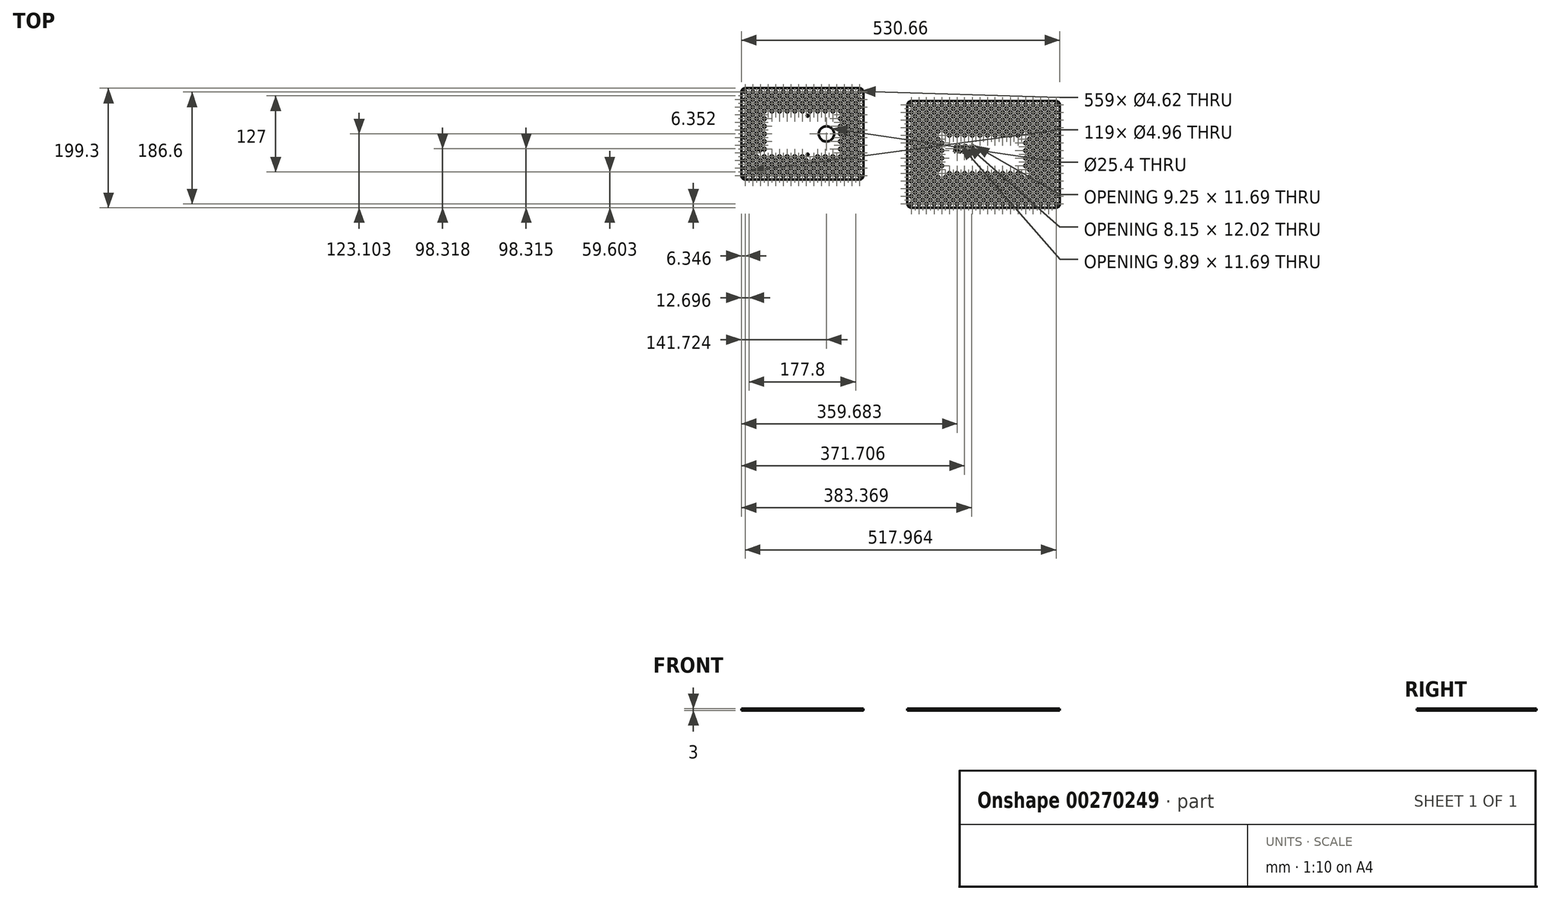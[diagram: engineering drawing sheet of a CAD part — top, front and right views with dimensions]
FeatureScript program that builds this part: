
annotation { "Feature Type Name" : "Feature", "Feature Type Description" : "" }
export const myFeature = defineFeature(function(context is Context, id is Id, definition is map)
    precondition{}
    {
        {
            var Q0;
            Q0=qCreatedBy(makeId("Top.planeOp"),FACE);
            var sketch = newSketch(context, id + "F0", { "sketchPlane" : qUnion([Q0])});
            skLineSegment(sketch, "E0.bottom", {"start": v(-123.65, 33.77) * mm, "end": v(-33.15, 33.77) * mm});
            skLineSegment(sketch, "E0.top", {"start": v(-123.65, -51.03) * mm, "end": v(-106.77, -51.03) * mm});
            skLineSegment(sketch, "E0.left", {"start": v(-123.65, 33.77) * mm, "end": v(-123.65, -51.03) * mm});
            skLineSegment(sketch, "E0.right", {"start": v(-33.15, 33.77) * mm, "end": v(-33.15, 7.9) * mm});
            skLineSegment(sketch, "E1", {"start": v(-38.6, 21.73) * mm, "end": v(-38.6, -43.27) * mm});
            skLineSegment(sketch, "E2", {"start": v(-117.57, 21.73) * mm, "end": v(-38.6, 21.73) * mm});
            skLineSegment(sketch, "E3", {"start": v(-38.6, 21.73) * mm, "end": v(-38.6, 33.77) * mm});
            skLineSegment(sketch, "E4", {"start": v(-38.6, -43.27) * mm, "end": v(-38.6, -51.03) * mm});
            skLineSegment(sketch, "E5", {"start": v(-37.02, -43.27) * mm, "end": v(-38.6, -43.27) * mm});
            skLineSegment(sketch, "E6", {"start": v(-117.57, -43.27) * mm, "end": v(-117.57, -36.09) * mm});
            skLineSegment(sketch, "E7", {"start": v(-117.57, -36.09) * mm, "end": v(-117.57, 21.73) * mm});
            skCircle(sketch, "E8", {"center": v(-117.57, -36.09) * mm, "radius": 1.59 * mm});
            skCircle(sketch, "E9", {"center": v(-38.6, 21.73) * mm, "radius": 1.59 * mm});
            skCircle(sketch, "E10", {"center": v(-38.6, -43.27) * mm, "radius": 1.59 * mm});
            skLineSegment(sketch, "E11.bottom", {"start": v(-142.7, 67.57) * mm, "end": v(47.8, 67.57) * mm});
            skLineSegment(sketch, "E11.top", {"start": v(-142.7, -84.83) * mm, "end": v(47.8, -84.83) * mm});
            skLineSegment(sketch, "E11.left", {"start": v(-149.05, 61.22) * mm, "end": v(-149.05, -78.48) * mm});
            skLineSegment(sketch, "E11.right", {"start": v(54.15, 61.22) * mm, "end": v(54.15, -78.48) * mm});
            skPoint(sketch, "E12", {"position": v(-106.77, -51.03) * mm});
            skPoint(sketch, "E13", {"position": v(-98.6, -51.03) * mm});
            skLineSegment(sketch, "E14.trimOffspring", {"start": v(-98.6, -51.03) * mm, "end": v(-33.15, -51.03) * mm});
            skPoint(sketch, "E15", {"position": v(-33.15, 7.9) * mm});
            skPoint(sketch, "E16", {"position": v(-33.15, -0.84) * mm});
            skLineSegment(sketch, "E17.trimOffspring", {"start": v(-33.15, -0.84) * mm, "end": v(-33.15, -51.03) * mm});
            skLineSegment(sketch, "E18", {"start": v(-149.05, -8.63) * mm, "end": v(-123.65, -8.63) * mm});
            skPoint(sketch, "E19", {"position": v(-90.24, -8.63) * mm});
            skPoint(sketch, "E20", {"position": v(-81.22, -8.63) * mm});
            skPoint(sketch, "E21", {"position": v(-47.45, -38.9) * mm});
            skLineSegment(sketch, "E22.trimOffspring", {"start": v(-81.22, -8.63) * mm, "end": v(-38.6, -8.63) * mm});
            skLineSegment(sketch, "E23.trimOffspring", {"start": v(-47.45, -38.9) * mm, "end": v(-47.45, -84.83) * mm});
            skLineSegment(sketch, "E24.trimOffspring", {"start": v(-117.57, -8.63) * mm, "end": v(-90.24, -8.63) * mm});
            skLineSegment(sketch, "E25.trimOffspring", {"start": v(-33.15, -8.63) * mm, "end": v(54.15, -8.63) * mm});
            skCircle(sketch, "E26", {"center": v(-7.33, -8.63) * mm, "radius": 12.7 * mm});
            skPoint(sketch, "E27.visualSharp", {"position": v(54.15, 67.57) * mm});
            skArc(sketch, "E27.filletArc", {"start": v(54.15, 61.22) * mm, "mid": v(52.29, 65.71) * mm, "end": v(47.8, 67.57) * mm});
            skPoint(sketch, "E28.visualSharp", {"position": v(-149.05, 67.57) * mm});
            skArc(sketch, "E28.filletArc", {"start": v(-142.7, 67.57) * mm, "mid": v(-147.2, 65.71) * mm, "end": v(-149.05, 61.22) * mm});
            skPoint(sketch, "E29.visualSharp", {"position": v(-149.05, -84.83) * mm});
            skArc(sketch, "E29.filletArc", {"start": v(-149.05, -78.48) * mm, "mid": v(-147.2, -82.97) * mm, "end": v(-142.7, -84.83) * mm});
            skPoint(sketch, "E30.visualSharp", {"position": v(54.15, -84.83) * mm});
            skArc(sketch, "E30.filletArc", {"start": v(47.8, -84.83) * mm, "mid": v(52.29, -82.97) * mm, "end": v(54.15, -78.48) * mm});
            skSolve(sketch);
        }
        {
            var Q0;
            Q0 = qSketchRegion(id + "F0", true);
            extrude(context, id + "F1", {"entities" : qUnion([Q0]), "depth" : 3 * mm});
        }
        {
            var Q0;
            Q0=makeQuery(id+"F1.opExtrude","CAP_FACE",FACE,{"disambiguationData":[OSD([sQuery(id+"F0.wireOp",EDGE,"E8"),sQuery(id+"F0.wireOp",EDGE,"E9"),sQuery(id+"F0.wireOp",EDGE,"E10"),sQuery(id+"F0.wireOp",EDGE,"E11.bottom"),sQuery(id+"F0.wireOp",EDGE,"E11.top"),sQuery(id+"F0.wireOp",EDGE,"E11.left"),sQuery(id+"F0.wireOp",EDGE,"E11.right"),sQuery(id+"F0.wireOp",EDGE,"E26")])],"isStart":false});
            var sketch = newSketch(context, id + "F2", { "sketchPlane" : qUnion([Q0])});
            skCircle(sketch, "E31", {"center": v(-142.7, 61.22) * mm, "radius": 2.31 * mm});
            skLineSegment(sketch, "E32", {"start": v(-142.7, 61.22) * mm, "end": v(-142.7, 67.57) * mm});
            skLineSegment(sketch, "E33", {"start": v(-142.7, 61.22) * mm, "end": v(-149.05, 61.22) * mm});
            skCircle(sketch, "E34.0.1.0", {"center": v(-142.7, 48.52) * mm, "radius": 2.31 * mm});
            skCircle(sketch, "E34.0.2.0", {"center": v(-142.7, 35.82) * mm, "radius": 2.31 * mm});
            skCircle(sketch, "E34.0.3.0", {"center": v(-142.7, 23.12) * mm, "radius": 2.31 * mm});
            skCircle(sketch, "E34.0.4.0", {"center": v(-142.7, 10.42) * mm, "radius": 2.31 * mm});
            skCircle(sketch, "E34.0.5.0", {"center": v(-142.7, -2.28) * mm, "radius": 2.31 * mm});
            skCircle(sketch, "E34.0.6.0", {"center": v(-142.7, -14.98) * mm, "radius": 2.31 * mm});
            skCircle(sketch, "E34.0.7.0", {"center": v(-142.7, -27.68) * mm, "radius": 2.31 * mm});
            skCircle(sketch, "E34.0.8.0", {"center": v(-142.7, -40.38) * mm, "radius": 2.31 * mm});
            skCircle(sketch, "E34.0.9.0", {"center": v(-142.7, -53.08) * mm, "radius": 2.31 * mm});
            skCircle(sketch, "E34.0.10.0", {"center": v(-142.7, -65.78) * mm, "radius": 2.31 * mm});
            skCircle(sketch, "E34.0.11.0", {"center": v(-142.7, -78.48) * mm, "radius": 2.31 * mm});
            skCircle(sketch, "E34.1.0.0", {"center": v(-130, 61.22) * mm, "radius": 2.31 * mm});
            skCircle(sketch, "E34.1.1.0", {"center": v(-130, 48.52) * mm, "radius": 2.31 * mm});
            skCircle(sketch, "E34.1.2.0", {"center": v(-130, 35.82) * mm, "radius": 2.31 * mm});
            skCircle(sketch, "E34.1.3.0", {"center": v(-130, 23.12) * mm, "radius": 2.31 * mm});
            skCircle(sketch, "E34.1.4.0", {"center": v(-130, 10.42) * mm, "radius": 2.31 * mm});
            skCircle(sketch, "E34.1.5.0", {"center": v(-130, -2.28) * mm, "radius": 2.31 * mm});
            skCircle(sketch, "E34.1.6.0", {"center": v(-130, -14.98) * mm, "radius": 2.31 * mm});
            skCircle(sketch, "E34.1.7.0", {"center": v(-130, -27.68) * mm, "radius": 2.31 * mm});
            skCircle(sketch, "E34.1.8.0", {"center": v(-130, -40.38) * mm, "radius": 2.31 * mm});
            skCircle(sketch, "E34.1.9.0", {"center": v(-130, -53.08) * mm, "radius": 2.31 * mm});
            skCircle(sketch, "E34.1.10.0", {"center": v(-130, -65.78) * mm, "radius": 2.31 * mm});
            skCircle(sketch, "E34.1.11.0", {"center": v(-130, -78.48) * mm, "radius": 2.31 * mm});
            skCircle(sketch, "E34.2.0.0", {"center": v(-117.3, 61.22) * mm, "radius": 2.31 * mm});
            skCircle(sketch, "E34.2.1.0", {"center": v(-117.3, 48.52) * mm, "radius": 2.31 * mm});
            skCircle(sketch, "E34.2.2.0", {"center": v(-117.3, 35.82) * mm, "radius": 2.31 * mm});
            skCircle(sketch, "E34.2.3.0", {"center": v(-117.3, 23.12) * mm, "radius": 2.31 * mm});
            skCircle(sketch, "E34.2.4.0", {"center": v(-117.3, 10.42) * mm, "radius": 2.31 * mm});
            skCircle(sketch, "E34.2.5.0", {"center": v(-117.3, -2.28) * mm, "radius": 2.31 * mm});
            skCircle(sketch, "E34.2.6.0", {"center": v(-117.3, -14.98) * mm, "radius": 2.31 * mm});
            skCircle(sketch, "E34.2.7.0", {"center": v(-117.3, -27.68) * mm, "radius": 2.31 * mm});
            skCircle(sketch, "E34.2.9.0", {"center": v(-117.3, -53.08) * mm, "radius": 2.31 * mm});
            skCircle(sketch, "E34.2.10.0", {"center": v(-117.3, -65.78) * mm, "radius": 2.31 * mm});
            skCircle(sketch, "E34.2.11.0", {"center": v(-117.3, -78.48) * mm, "radius": 2.31 * mm});
            skCircle(sketch, "E34.3.0.0", {"center": v(-104.6, 61.22) * mm, "radius": 2.31 * mm});
            skCircle(sketch, "E34.3.1.0", {"center": v(-104.6, 48.52) * mm, "radius": 2.31 * mm});
            skCircle(sketch, "E34.3.2.0", {"center": v(-104.6, 35.82) * mm, "radius": 2.31 * mm});
            skCircle(sketch, "E34.3.9.0", {"center": v(-104.6, -53.08) * mm, "radius": 2.31 * mm});
            skCircle(sketch, "E34.3.10.0", {"center": v(-104.6, -65.78) * mm, "radius": 2.31 * mm});
            skCircle(sketch, "E34.3.11.0", {"center": v(-104.6, -78.48) * mm, "radius": 2.31 * mm});
            skCircle(sketch, "E34.4.0.0", {"center": v(-91.9, 61.22) * mm, "radius": 2.31 * mm});
            skCircle(sketch, "E34.4.1.0", {"center": v(-91.9, 48.52) * mm, "radius": 2.31 * mm});
            skCircle(sketch, "E34.4.2.0", {"center": v(-91.9, 35.82) * mm, "radius": 2.31 * mm});
            skCircle(sketch, "E34.4.9.0", {"center": v(-91.9, -53.08) * mm, "radius": 2.31 * mm});
            skCircle(sketch, "E34.4.10.0", {"center": v(-91.9, -65.78) * mm, "radius": 2.31 * mm});
            skCircle(sketch, "E34.4.11.0", {"center": v(-91.9, -78.48) * mm, "radius": 2.31 * mm});
            skCircle(sketch, "E34.5.0.0", {"center": v(-79.2, 61.22) * mm, "radius": 2.31 * mm});
            skCircle(sketch, "E34.5.1.0", {"center": v(-79.2, 48.52) * mm, "radius": 2.31 * mm});
            skCircle(sketch, "E34.5.2.0", {"center": v(-79.2, 35.82) * mm, "radius": 2.31 * mm});
            skCircle(sketch, "E34.5.9.0", {"center": v(-79.2, -53.08) * mm, "radius": 2.31 * mm});
            skCircle(sketch, "E34.5.10.0", {"center": v(-79.2, -65.78) * mm, "radius": 2.31 * mm});
            skCircle(sketch, "E34.5.11.0", {"center": v(-79.2, -78.48) * mm, "radius": 2.31 * mm});
            skCircle(sketch, "E34.6.0.0", {"center": v(-66.5, 61.22) * mm, "radius": 2.31 * mm});
            skCircle(sketch, "E34.6.1.0", {"center": v(-66.5, 48.52) * mm, "radius": 2.31 * mm});
            skCircle(sketch, "E34.6.2.0", {"center": v(-66.5, 35.82) * mm, "radius": 2.31 * mm});
            skCircle(sketch, "E34.6.9.0", {"center": v(-66.5, -53.08) * mm, "radius": 2.31 * mm});
            skCircle(sketch, "E34.6.10.0", {"center": v(-66.5, -65.78) * mm, "radius": 2.31 * mm});
            skCircle(sketch, "E34.6.11.0", {"center": v(-66.5, -78.48) * mm, "radius": 2.31 * mm});
            skCircle(sketch, "E34.7.0.0", {"center": v(-53.8, 61.22) * mm, "radius": 2.31 * mm});
            skCircle(sketch, "E34.7.1.0", {"center": v(-53.8, 48.52) * mm, "radius": 2.31 * mm});
            skCircle(sketch, "E34.7.2.0", {"center": v(-53.8, 35.82) * mm, "radius": 2.31 * mm});
            skCircle(sketch, "E34.7.9.0", {"center": v(-53.8, -53.08) * mm, "radius": 2.31 * mm});
            skCircle(sketch, "E34.7.10.0", {"center": v(-53.8, -65.78) * mm, "radius": 2.31 * mm});
            skCircle(sketch, "E34.7.11.0", {"center": v(-53.8, -78.48) * mm, "radius": 2.31 * mm});
            skCircle(sketch, "E34.8.0.0", {"center": v(-41.1, 61.22) * mm, "radius": 2.31 * mm});
            skCircle(sketch, "E34.8.1.0", {"center": v(-41.1, 48.52) * mm, "radius": 2.31 * mm});
            skCircle(sketch, "E34.8.2.0", {"center": v(-41.1, 35.82) * mm, "radius": 2.31 * mm});
            skCircle(sketch, "E34.8.9.0", {"center": v(-41.1, -53.08) * mm, "radius": 2.31 * mm});
            skCircle(sketch, "E34.8.10.0", {"center": v(-41.1, -65.78) * mm, "radius": 2.31 * mm});
            skCircle(sketch, "E34.8.11.0", {"center": v(-41.1, -78.48) * mm, "radius": 2.31 * mm});
            skCircle(sketch, "E34.9.0.0", {"center": v(-28.4, 61.22) * mm, "radius": 2.31 * mm});
            skCircle(sketch, "E34.9.1.0", {"center": v(-28.4, 48.52) * mm, "radius": 2.31 * mm});
            skCircle(sketch, "E34.9.2.0", {"center": v(-28.4, 35.82) * mm, "radius": 2.31 * mm});
            skCircle(sketch, "E34.9.9.0", {"center": v(-28.4, -53.08) * mm, "radius": 2.31 * mm});
            skCircle(sketch, "E34.9.10.0", {"center": v(-28.4, -65.78) * mm, "radius": 2.31 * mm});
            skCircle(sketch, "E34.9.11.0", {"center": v(-28.4, -78.48) * mm, "radius": 2.31 * mm});
            skCircle(sketch, "E34.10.0.0", {"center": v(-15.7, 61.22) * mm, "radius": 2.31 * mm});
            skCircle(sketch, "E34.10.1.0", {"center": v(-15.7, 48.52) * mm, "radius": 2.31 * mm});
            skCircle(sketch, "E34.10.2.0", {"center": v(-15.7, 35.82) * mm, "radius": 2.31 * mm});
            skCircle(sketch, "E34.10.9.0", {"center": v(-15.7, -53.08) * mm, "radius": 2.31 * mm});
            skCircle(sketch, "E34.10.10.0", {"center": v(-15.7, -65.78) * mm, "radius": 2.31 * mm});
            skCircle(sketch, "E34.10.11.0", {"center": v(-15.7, -78.48) * mm, "radius": 2.31 * mm});
            skCircle(sketch, "E34.11.0.0", {"center": v(-3, 61.22) * mm, "radius": 2.31 * mm});
            skCircle(sketch, "E34.11.1.0", {"center": v(-3, 48.52) * mm, "radius": 2.31 * mm});
            skCircle(sketch, "E34.11.2.0", {"center": v(-3, 35.82) * mm, "radius": 2.31 * mm});
            skCircle(sketch, "E34.11.9.0", {"center": v(-3, -53.08) * mm, "radius": 2.31 * mm});
            skCircle(sketch, "E34.11.10.0", {"center": v(-3, -65.78) * mm, "radius": 2.31 * mm});
            skCircle(sketch, "E34.11.11.0", {"center": v(-3, -78.48) * mm, "radius": 2.31 * mm});
            skCircle(sketch, "E34.12.0.0", {"center": v(9.7, 61.22) * mm, "radius": 2.31 * mm});
            skCircle(sketch, "E34.12.1.0", {"center": v(9.7, 48.52) * mm, "radius": 2.31 * mm});
            skCircle(sketch, "E34.12.2.0", {"center": v(9.7, 35.82) * mm, "radius": 2.31 * mm});
            skCircle(sketch, "E34.12.9.0", {"center": v(9.7, -53.08) * mm, "radius": 2.31 * mm});
            skCircle(sketch, "E34.12.10.0", {"center": v(9.7, -65.78) * mm, "radius": 2.31 * mm});
            skCircle(sketch, "E34.12.11.0", {"center": v(9.7, -78.48) * mm, "radius": 2.31 * mm});
            skCircle(sketch, "E34.13.0.0", {"center": v(22.4, 61.22) * mm, "radius": 2.31 * mm});
            skCircle(sketch, "E34.13.1.0", {"center": v(22.4, 48.52) * mm, "radius": 2.31 * mm});
            skCircle(sketch, "E34.13.2.0", {"center": v(22.4, 35.82) * mm, "radius": 2.31 * mm});
            skCircle(sketch, "E34.13.3.0", {"center": v(22.4, 23.12) * mm, "radius": 2.31 * mm});
            skCircle(sketch, "E34.13.4.0", {"center": v(22.4, 10.42) * mm, "radius": 2.31 * mm});
            skCircle(sketch, "E34.13.5.0", {"center": v(22.4, -2.28) * mm, "radius": 2.31 * mm});
            skCircle(sketch, "E34.13.6.0", {"center": v(22.4, -14.98) * mm, "radius": 2.31 * mm});
            skCircle(sketch, "E34.13.7.0", {"center": v(22.4, -27.68) * mm, "radius": 2.31 * mm});
            skCircle(sketch, "E34.13.8.0", {"center": v(22.4, -40.38) * mm, "radius": 2.31 * mm});
            skCircle(sketch, "E34.13.9.0", {"center": v(22.4, -53.08) * mm, "radius": 2.31 * mm});
            skCircle(sketch, "E34.13.10.0", {"center": v(22.4, -65.78) * mm, "radius": 2.31 * mm});
            skCircle(sketch, "E34.13.11.0", {"center": v(22.4, -78.48) * mm, "radius": 2.31 * mm});
            skCircle(sketch, "E34.14.0.0", {"center": v(35.1, 61.22) * mm, "radius": 2.31 * mm});
            skCircle(sketch, "E34.14.1.0", {"center": v(35.1, 48.52) * mm, "radius": 2.31 * mm});
            skCircle(sketch, "E34.14.2.0", {"center": v(35.1, 35.82) * mm, "radius": 2.31 * mm});
            skCircle(sketch, "E34.14.3.0", {"center": v(35.1, 23.12) * mm, "radius": 2.31 * mm});
            skCircle(sketch, "E34.14.4.0", {"center": v(35.1, 10.42) * mm, "radius": 2.31 * mm});
            skCircle(sketch, "E34.14.5.0", {"center": v(35.1, -2.28) * mm, "radius": 2.31 * mm});
            skCircle(sketch, "E34.14.6.0", {"center": v(35.1, -14.98) * mm, "radius": 2.31 * mm});
            skCircle(sketch, "E34.14.7.0", {"center": v(35.1, -27.68) * mm, "radius": 2.31 * mm});
            skCircle(sketch, "E34.14.8.0", {"center": v(35.1, -40.38) * mm, "radius": 2.31 * mm});
            skCircle(sketch, "E34.14.9.0", {"center": v(35.1, -53.08) * mm, "radius": 2.31 * mm});
            skCircle(sketch, "E34.14.10.0", {"center": v(35.1, -65.78) * mm, "radius": 2.31 * mm});
            skCircle(sketch, "E34.14.11.0", {"center": v(35.1, -78.48) * mm, "radius": 2.31 * mm});
            skCircle(sketch, "E34.15.0.0", {"center": v(47.8, 61.22) * mm, "radius": 2.31 * mm});
            skCircle(sketch, "E34.15.1.0", {"center": v(47.8, 48.52) * mm, "radius": 2.31 * mm});
            skCircle(sketch, "E34.15.2.0", {"center": v(47.8, 35.82) * mm, "radius": 2.31 * mm});
            skCircle(sketch, "E34.15.3.0", {"center": v(47.8, 23.12) * mm, "radius": 2.31 * mm});
            skCircle(sketch, "E34.15.4.0", {"center": v(47.8, 10.42) * mm, "radius": 2.31 * mm});
            skCircle(sketch, "E34.15.5.0", {"center": v(47.8, -2.28) * mm, "radius": 2.31 * mm});
            skCircle(sketch, "E34.15.6.0", {"center": v(47.8, -14.98) * mm, "radius": 2.31 * mm});
            skCircle(sketch, "E34.15.7.0", {"center": v(47.8, -27.68) * mm, "radius": 2.31 * mm});
            skCircle(sketch, "E34.15.8.0", {"center": v(47.8, -40.38) * mm, "radius": 2.31 * mm});
            skCircle(sketch, "E34.15.9.0", {"center": v(47.8, -53.08) * mm, "radius": 2.31 * mm});
            skCircle(sketch, "E34.15.10.0", {"center": v(47.8, -65.78) * mm, "radius": 2.31 * mm});
            skCircle(sketch, "E34.15.11.0", {"center": v(47.8, -78.48) * mm, "radius": 2.31 * mm});
            skLineSegment(sketch, "E34.direction1", {"start": v(-142.7, 61.22) * mm, "end": v(-130, 61.22) * mm, "construction": true});
            skLineSegment(sketch, "E34.direction2", {"start": v(-142.7, 61.22) * mm, "end": v(-142.7, 48.52) * mm, "construction": true});
            skLineSegment(sketch, "E35", {"start": v(47.8, 61.22) * mm, "end": v(54.15, 61.22) * mm});
            skLineSegment(sketch, "E36", {"start": v(-142.7, -78.48) * mm, "end": v(-142.7, -84.83) * mm});
            skCircle(sketch, "E37", {"center": v(-136.35, 54.87) * mm, "radius": 2.48 * mm});
            skCircle(sketch, "E38.0.1.0", {"center": v(-136.35, 42.17) * mm, "radius": 2.48 * mm});
            skCircle(sketch, "E38.0.2.0", {"center": v(-136.35, 29.47) * mm, "radius": 2.48 * mm});
            skCircle(sketch, "E38.0.3.0", {"center": v(-136.35, 16.77) * mm, "radius": 2.48 * mm});
            skCircle(sketch, "E38.0.4.0", {"center": v(-136.35, 4.07) * mm, "radius": 2.48 * mm});
            skCircle(sketch, "E38.0.5.0", {"center": v(-136.35, -8.63) * mm, "radius": 2.48 * mm});
            skCircle(sketch, "E38.0.6.0", {"center": v(-136.35, -21.33) * mm, "radius": 2.48 * mm});
            skCircle(sketch, "E38.0.7.0", {"center": v(-136.35, -34.03) * mm, "radius": 2.48 * mm});
            skCircle(sketch, "E38.0.8.0", {"center": v(-136.35, -46.73) * mm, "radius": 2.48 * mm});
            skCircle(sketch, "E38.0.9.0", {"center": v(-136.35, -59.43) * mm, "radius": 2.48 * mm});
            skCircle(sketch, "E38.0.10.0", {"center": v(-136.35, -72.13) * mm, "radius": 2.48 * mm});
            skCircle(sketch, "E38.1.0.0", {"center": v(-123.65, 54.87) * mm, "radius": 2.48 * mm});
            skCircle(sketch, "E38.1.1.0", {"center": v(-123.65, 42.17) * mm, "radius": 2.48 * mm});
            skCircle(sketch, "E38.1.2.0", {"center": v(-123.65, 29.47) * mm, "radius": 2.48 * mm});
            skCircle(sketch, "E38.1.3.0", {"center": v(-123.65, 16.77) * mm, "radius": 2.48 * mm});
            skCircle(sketch, "E38.1.4.0", {"center": v(-123.65, 4.07) * mm, "radius": 2.48 * mm});
            skCircle(sketch, "E38.1.5.0", {"center": v(-123.65, -8.63) * mm, "radius": 2.48 * mm});
            skCircle(sketch, "E38.1.6.0", {"center": v(-123.65, -21.33) * mm, "radius": 2.48 * mm});
            skCircle(sketch, "E38.1.7.0", {"center": v(-123.65, -34.03) * mm, "radius": 2.48 * mm});
            skCircle(sketch, "E38.1.8.0", {"center": v(-123.65, -46.73) * mm, "radius": 2.48 * mm});
            skCircle(sketch, "E38.1.9.0", {"center": v(-123.65, -59.43) * mm, "radius": 2.48 * mm});
            skCircle(sketch, "E38.1.10.0", {"center": v(-123.65, -72.13) * mm, "radius": 2.48 * mm});
            skCircle(sketch, "E38.2.0.0", {"center": v(-110.95, 54.87) * mm, "radius": 2.48 * mm});
            skCircle(sketch, "E38.2.1.0", {"center": v(-110.95, 42.17) * mm, "radius": 2.48 * mm});
            skCircle(sketch, "E38.2.2.0", {"center": v(-110.95, 29.47) * mm, "radius": 2.48 * mm});
            skCircle(sketch, "E38.2.3.0", {"center": v(-110.95, 16.77) * mm, "radius": 2.48 * mm});
            skCircle(sketch, "E38.2.4.0", {"center": v(-110.95, 4.07) * mm, "radius": 2.48 * mm});
            skCircle(sketch, "E38.2.5.0", {"center": v(-110.95, -8.63) * mm, "radius": 2.48 * mm});
            skCircle(sketch, "E38.2.6.0", {"center": v(-110.95, -21.33) * mm, "radius": 2.48 * mm});
            skCircle(sketch, "E38.2.7.0", {"center": v(-110.95, -34.03) * mm, "radius": 2.48 * mm});
            skCircle(sketch, "E38.2.8.0", {"center": v(-110.95, -46.73) * mm, "radius": 2.48 * mm});
            skCircle(sketch, "E38.2.9.0", {"center": v(-110.95, -59.43) * mm, "radius": 2.48 * mm});
            skCircle(sketch, "E38.2.10.0", {"center": v(-110.95, -72.13) * mm, "radius": 2.48 * mm});
            skCircle(sketch, "E38.3.0.0", {"center": v(-98.25, 54.87) * mm, "radius": 2.48 * mm});
            skCircle(sketch, "E38.3.1.0", {"center": v(-98.25, 42.17) * mm, "radius": 2.48 * mm});
            skCircle(sketch, "E38.3.2.0", {"center": v(-98.25, 29.47) * mm, "radius": 2.48 * mm});
            skCircle(sketch, "E38.3.8.0", {"center": v(-98.25, -46.73) * mm, "radius": 2.48 * mm});
            skCircle(sketch, "E38.3.9.0", {"center": v(-98.25, -59.43) * mm, "radius": 2.48 * mm});
            skCircle(sketch, "E38.3.10.0", {"center": v(-98.25, -72.13) * mm, "radius": 2.48 * mm});
            skCircle(sketch, "E38.4.0.0", {"center": v(-85.55, 54.87) * mm, "radius": 2.48 * mm});
            skCircle(sketch, "E38.4.1.0", {"center": v(-85.55, 42.17) * mm, "radius": 2.48 * mm});
            skCircle(sketch, "E38.4.2.0", {"center": v(-85.55, 29.47) * mm, "radius": 2.48 * mm});
            skCircle(sketch, "E38.4.8.0", {"center": v(-85.55, -46.73) * mm, "radius": 2.48 * mm});
            skCircle(sketch, "E38.4.9.0", {"center": v(-85.55, -59.43) * mm, "radius": 2.48 * mm});
            skCircle(sketch, "E38.4.10.0", {"center": v(-85.55, -72.13) * mm, "radius": 2.48 * mm});
            skCircle(sketch, "E38.5.0.0", {"center": v(-72.85, 54.87) * mm, "radius": 2.48 * mm});
            skCircle(sketch, "E38.5.1.0", {"center": v(-72.85, 42.17) * mm, "radius": 2.48 * mm});
            skCircle(sketch, "E38.5.2.0", {"center": v(-72.85, 29.47) * mm, "radius": 2.48 * mm});
            skCircle(sketch, "E38.5.8.0", {"center": v(-72.85, -46.73) * mm, "radius": 2.48 * mm});
            skCircle(sketch, "E38.5.9.0", {"center": v(-72.85, -59.43) * mm, "radius": 2.48 * mm});
            skCircle(sketch, "E38.5.10.0", {"center": v(-72.85, -72.13) * mm, "radius": 2.48 * mm});
            skCircle(sketch, "E38.6.0.0", {"center": v(-60.15, 54.87) * mm, "radius": 2.48 * mm});
            skCircle(sketch, "E38.6.1.0", {"center": v(-60.15, 42.17) * mm, "radius": 2.48 * mm});
            skCircle(sketch, "E38.6.2.0", {"center": v(-60.15, 29.47) * mm, "radius": 2.48 * mm});
            skCircle(sketch, "E38.6.8.0", {"center": v(-60.15, -46.73) * mm, "radius": 2.48 * mm});
            skCircle(sketch, "E38.6.9.0", {"center": v(-60.15, -59.43) * mm, "radius": 2.48 * mm});
            skCircle(sketch, "E38.6.10.0", {"center": v(-60.15, -72.13) * mm, "radius": 2.48 * mm});
            skCircle(sketch, "E38.7.0.0", {"center": v(-47.45, 54.87) * mm, "radius": 2.48 * mm});
            skCircle(sketch, "E38.7.1.0", {"center": v(-47.45, 42.17) * mm, "radius": 2.48 * mm});
            skCircle(sketch, "E38.7.2.0", {"center": v(-47.45, 29.47) * mm, "radius": 2.48 * mm});
            skCircle(sketch, "E38.7.8.0", {"center": v(-47.45, -46.73) * mm, "radius": 2.48 * mm});
            skCircle(sketch, "E38.7.9.0", {"center": v(-47.45, -59.43) * mm, "radius": 2.48 * mm});
            skCircle(sketch, "E38.7.10.0", {"center": v(-47.45, -72.13) * mm, "radius": 2.48 * mm});
            skCircle(sketch, "E38.8.0.0", {"center": v(-34.75, 54.87) * mm, "radius": 2.48 * mm});
            skCircle(sketch, "E38.8.1.0", {"center": v(-34.75, 42.17) * mm, "radius": 2.48 * mm});
            skCircle(sketch, "E38.8.2.0", {"center": v(-34.75, 29.47) * mm, "radius": 2.48 * mm});
            skCircle(sketch, "E38.8.9.0", {"center": v(-34.75, -59.43) * mm, "radius": 2.48 * mm});
            skCircle(sketch, "E38.8.10.0", {"center": v(-34.75, -72.13) * mm, "radius": 2.48 * mm});
            skCircle(sketch, "E38.9.0.0", {"center": v(-22.05, 54.87) * mm, "radius": 2.48 * mm});
            skCircle(sketch, "E38.9.1.0", {"center": v(-22.05, 42.17) * mm, "radius": 2.48 * mm});
            skCircle(sketch, "E38.9.2.0", {"center": v(-22.05, 29.47) * mm, "radius": 2.48 * mm});
            skCircle(sketch, "E38.9.8.0", {"center": v(-22.05, -46.73) * mm, "radius": 2.48 * mm});
            skCircle(sketch, "E38.9.9.0", {"center": v(-22.05, -59.43) * mm, "radius": 2.48 * mm});
            skCircle(sketch, "E38.9.10.0", {"center": v(-22.05, -72.13) * mm, "radius": 2.48 * mm});
            skCircle(sketch, "E38.10.0.0", {"center": v(-9.35, 54.87) * mm, "radius": 2.48 * mm});
            skCircle(sketch, "E38.10.1.0", {"center": v(-9.35, 42.17) * mm, "radius": 2.48 * mm});
            skCircle(sketch, "E38.10.2.0", {"center": v(-9.35, 29.47) * mm, "radius": 2.48 * mm});
            skCircle(sketch, "E38.10.8.0", {"center": v(-9.35, -46.73) * mm, "radius": 2.48 * mm});
            skCircle(sketch, "E38.10.9.0", {"center": v(-9.35, -59.43) * mm, "radius": 2.48 * mm});
            skCircle(sketch, "E38.10.10.0", {"center": v(-9.35, -72.13) * mm, "radius": 2.48 * mm});
            skCircle(sketch, "E38.11.0.0", {"center": v(3.35, 54.87) * mm, "radius": 2.48 * mm});
            skCircle(sketch, "E38.11.1.0", {"center": v(3.35, 42.17) * mm, "radius": 2.48 * mm});
            skCircle(sketch, "E38.11.2.0", {"center": v(3.35, 29.47) * mm, "radius": 2.48 * mm});
            skCircle(sketch, "E38.11.8.0", {"center": v(3.35, -46.73) * mm, "radius": 2.48 * mm});
            skCircle(sketch, "E38.11.9.0", {"center": v(3.35, -59.43) * mm, "radius": 2.48 * mm});
            skCircle(sketch, "E38.11.10.0", {"center": v(3.35, -72.13) * mm, "radius": 2.48 * mm});
            skCircle(sketch, "E38.12.0.0", {"center": v(16.05, 54.87) * mm, "radius": 2.48 * mm});
            skCircle(sketch, "E38.12.1.0", {"center": v(16.05, 42.17) * mm, "radius": 2.48 * mm});
            skCircle(sketch, "E38.12.2.0", {"center": v(16.05, 29.47) * mm, "radius": 2.48 * mm});
            skCircle(sketch, "E38.12.3.0", {"center": v(16.05, 16.77) * mm, "radius": 2.48 * mm});
            skCircle(sketch, "E38.12.4.0", {"center": v(16.05, 4.07) * mm, "radius": 2.48 * mm});
            skCircle(sketch, "E38.12.5.0", {"center": v(16.05, -8.63) * mm, "radius": 2.48 * mm});
            skCircle(sketch, "E38.12.6.0", {"center": v(16.05, -21.33) * mm, "radius": 2.48 * mm});
            skCircle(sketch, "E38.12.7.0", {"center": v(16.05, -34.03) * mm, "radius": 2.48 * mm});
            skCircle(sketch, "E38.12.8.0", {"center": v(16.05, -46.73) * mm, "radius": 2.48 * mm});
            skCircle(sketch, "E38.12.9.0", {"center": v(16.05, -59.43) * mm, "radius": 2.48 * mm});
            skCircle(sketch, "E38.12.10.0", {"center": v(16.05, -72.13) * mm, "radius": 2.48 * mm});
            skCircle(sketch, "E38.13.0.0", {"center": v(28.75, 54.87) * mm, "radius": 2.48 * mm});
            skCircle(sketch, "E38.13.1.0", {"center": v(28.75, 42.17) * mm, "radius": 2.48 * mm});
            skCircle(sketch, "E38.13.2.0", {"center": v(28.75, 29.47) * mm, "radius": 2.48 * mm});
            skCircle(sketch, "E38.13.3.0", {"center": v(28.75, 16.77) * mm, "radius": 2.48 * mm});
            skCircle(sketch, "E38.13.4.0", {"center": v(28.75, 4.07) * mm, "radius": 2.48 * mm});
            skCircle(sketch, "E38.13.5.0", {"center": v(28.75, -8.63) * mm, "radius": 2.48 * mm});
            skCircle(sketch, "E38.13.6.0", {"center": v(28.75, -21.33) * mm, "radius": 2.48 * mm});
            skCircle(sketch, "E38.13.7.0", {"center": v(28.75, -34.03) * mm, "radius": 2.48 * mm});
            skCircle(sketch, "E38.13.8.0", {"center": v(28.75, -46.73) * mm, "radius": 2.48 * mm});
            skCircle(sketch, "E38.13.9.0", {"center": v(28.75, -59.43) * mm, "radius": 2.48 * mm});
            skCircle(sketch, "E38.13.10.0", {"center": v(28.75, -72.13) * mm, "radius": 2.48 * mm});
            skCircle(sketch, "E38.14.0.0", {"center": v(41.45, 54.87) * mm, "radius": 2.48 * mm});
            skCircle(sketch, "E38.14.1.0", {"center": v(41.45, 42.17) * mm, "radius": 2.48 * mm});
            skCircle(sketch, "E38.14.2.0", {"center": v(41.45, 29.47) * mm, "radius": 2.48 * mm});
            skCircle(sketch, "E38.14.3.0", {"center": v(41.45, 16.77) * mm, "radius": 2.48 * mm});
            skCircle(sketch, "E38.14.4.0", {"center": v(41.45, 4.07) * mm, "radius": 2.48 * mm});
            skCircle(sketch, "E38.14.5.0", {"center": v(41.45, -8.63) * mm, "radius": 2.48 * mm});
            skCircle(sketch, "E38.14.6.0", {"center": v(41.45, -21.33) * mm, "radius": 2.48 * mm});
            skCircle(sketch, "E38.14.7.0", {"center": v(41.45, -34.03) * mm, "radius": 2.48 * mm});
            skCircle(sketch, "E38.14.8.0", {"center": v(41.45, -46.73) * mm, "radius": 2.48 * mm});
            skCircle(sketch, "E38.14.9.0", {"center": v(41.45, -59.43) * mm, "radius": 2.48 * mm});
            skCircle(sketch, "E38.14.10.0", {"center": v(41.45, -72.13) * mm, "radius": 2.48 * mm});
            skLineSegment(sketch, "E38.direction1", {"start": v(-136.35, 54.87) * mm, "end": v(-123.65, 54.87) * mm, "construction": true});
            skLineSegment(sketch, "E38.direction2", {"start": v(-136.35, 54.87) * mm, "end": v(-136.35, 42.17) * mm, "construction": true});
            skSolve(sketch);
        }
        {
            var Q0;
            Q0 = qSketchRegion(id + "F2", true);
            extrude(context, id + "F3", {"entities" : qUnion([Q0]), "operationType" : NewBodyOperationType.REMOVE, "oppositeDirection" : true, "depth" : 25.4 * mm});
        }
        {
            var Q0;
            Q0=qCreatedBy(makeId("Top.planeOp"),FACE);
            var sketch = newSketch(context, id + "F4", { "sketchPlane" : qUnion([Q0])});
            skLineSegment(sketch, "E39.bottom", {"start": v(133.96, 46.07) * mm, "end": v(375.26, 46.07) * mm});
            skLineSegment(sketch, "E39.top", {"start": v(133.96, -131.73) * mm, "end": v(375.26, -131.73) * mm});
            skLineSegment(sketch, "E39.left", {"start": v(127.6, 39.72) * mm, "end": v(127.6, -125.38) * mm});
            skLineSegment(sketch, "E39.right", {"start": v(381.6, 39.72) * mm, "end": v(381.6, -125.38) * mm});
            skPoint(sketch, "E40.visualSharp", {"position": v(127.6, 46.07) * mm});
            skArc(sketch, "E40.filletArc", {"start": v(133.96, 46.07) * mm, "mid": v(129.47, 44.21) * mm, "end": v(127.6, 39.72) * mm});
            skPoint(sketch, "E41.visualSharp", {"position": v(381.6, 46.07) * mm});
            skArc(sketch, "E41.filletArc", {"start": v(381.6, 39.72) * mm, "mid": v(379.75, 44.21) * mm, "end": v(375.26, 46.07) * mm});
            skPoint(sketch, "E42.visualSharp", {"position": v(381.6, -131.73) * mm});
            skArc(sketch, "E42.filletArc", {"start": v(375.26, -131.73) * mm, "mid": v(379.75, -129.87) * mm, "end": v(381.6, -125.38) * mm});
            skPoint(sketch, "E43.visualSharp", {"position": v(127.6, -131.73) * mm});
            skArc(sketch, "E43.filletArc", {"start": v(127.6, -125.38) * mm, "mid": v(129.47, -129.87) * mm, "end": v(133.96, -131.73) * mm});
            skText(sketch, "E44", { "text": "K.S.A.", "fontName": "OpenSans-Italic.ttf"});
            skCircle(sketch, "E45", {"center": v(133.96, 39.72) * mm, "radius": 2.31 * mm});
            skLineSegment(sketch, "E46", {"start": v(133.96, 39.72) * mm, "end": v(133.96, 46.07) * mm});
            skLineSegment(sketch, "E47", {"start": v(133.96, 39.72) * mm, "end": v(127.6, 39.72) * mm});
            skCircle(sketch, "E48.0.1.0", {"center": v(133.96, 27.02) * mm, "radius": 2.31 * mm});
            skCircle(sketch, "E48.0.2.0", {"center": v(133.96, 14.32) * mm, "radius": 2.31 * mm});
            skCircle(sketch, "E48.0.3.0", {"center": v(133.96, 1.62) * mm, "radius": 2.31 * mm});
            skCircle(sketch, "E48.0.4.0", {"center": v(133.96, -11.08) * mm, "radius": 2.31 * mm});
            skCircle(sketch, "E48.0.5.0", {"center": v(133.96, -23.78) * mm, "radius": 2.31 * mm});
            skCircle(sketch, "E48.0.6.0", {"center": v(133.96, -36.48) * mm, "radius": 2.31 * mm});
            skCircle(sketch, "E48.0.7.0", {"center": v(133.96, -49.18) * mm, "radius": 2.31 * mm});
            skCircle(sketch, "E48.0.8.0", {"center": v(133.96, -61.88) * mm, "radius": 2.31 * mm});
            skCircle(sketch, "E48.0.9.0", {"center": v(133.96, -74.58) * mm, "radius": 2.31 * mm});
            skCircle(sketch, "E48.0.10.0", {"center": v(133.96, -87.28) * mm, "radius": 2.31 * mm});
            skCircle(sketch, "E48.0.11.0", {"center": v(133.96, -99.98) * mm, "radius": 2.31 * mm});
            skCircle(sketch, "E48.0.12.0", {"center": v(133.96, -112.68) * mm, "radius": 2.31 * mm});
            skCircle(sketch, "E48.0.13.0", {"center": v(133.96, -125.38) * mm, "radius": 2.31 * mm});
            skCircle(sketch, "E48.1.0.0", {"center": v(146.66, 39.72) * mm, "radius": 2.31 * mm});
            skCircle(sketch, "E48.1.1.0", {"center": v(146.66, 27.02) * mm, "radius": 2.31 * mm});
            skCircle(sketch, "E48.1.2.0", {"center": v(146.66, 14.32) * mm, "radius": 2.31 * mm});
            skCircle(sketch, "E48.1.3.0", {"center": v(146.66, 1.62) * mm, "radius": 2.31 * mm});
            skCircle(sketch, "E48.1.4.0", {"center": v(146.66, -11.08) * mm, "radius": 2.31 * mm});
            skCircle(sketch, "E48.1.5.0", {"center": v(146.66, -23.78) * mm, "radius": 2.31 * mm});
            skCircle(sketch, "E48.1.6.0", {"center": v(146.66, -36.48) * mm, "radius": 2.31 * mm});
            skCircle(sketch, "E48.1.7.0", {"center": v(146.66, -49.18) * mm, "radius": 2.31 * mm});
            skCircle(sketch, "E48.1.8.0", {"center": v(146.66, -61.88) * mm, "radius": 2.31 * mm});
            skCircle(sketch, "E48.1.9.0", {"center": v(146.66, -74.58) * mm, "radius": 2.31 * mm});
            skCircle(sketch, "E48.1.10.0", {"center": v(146.66, -87.28) * mm, "radius": 2.31 * mm});
            skCircle(sketch, "E48.1.11.0", {"center": v(146.66, -99.98) * mm, "radius": 2.31 * mm});
            skCircle(sketch, "E48.1.12.0", {"center": v(146.66, -112.68) * mm, "radius": 2.31 * mm});
            skCircle(sketch, "E48.1.13.0", {"center": v(146.66, -125.38) * mm, "radius": 2.31 * mm});
            skCircle(sketch, "E48.2.0.0", {"center": v(159.36, 39.72) * mm, "radius": 2.31 * mm});
            skCircle(sketch, "E48.2.1.0", {"center": v(159.36, 27.02) * mm, "radius": 2.31 * mm});
            skCircle(sketch, "E48.2.2.0", {"center": v(159.36, 14.32) * mm, "radius": 2.31 * mm});
            skCircle(sketch, "E48.2.3.0", {"center": v(159.36, 1.62) * mm, "radius": 2.31 * mm});
            skCircle(sketch, "E48.2.4.0", {"center": v(159.36, -11.08) * mm, "radius": 2.31 * mm});
            skCircle(sketch, "E48.2.5.0", {"center": v(159.36, -23.78) * mm, "radius": 2.31 * mm});
            skCircle(sketch, "E48.2.6.0", {"center": v(159.36, -36.48) * mm, "radius": 2.31 * mm});
            skCircle(sketch, "E48.2.7.0", {"center": v(159.36, -49.18) * mm, "radius": 2.31 * mm});
            skCircle(sketch, "E48.2.8.0", {"center": v(159.36, -61.88) * mm, "radius": 2.31 * mm});
            skCircle(sketch, "E48.2.9.0", {"center": v(159.36, -74.58) * mm, "radius": 2.31 * mm});
            skCircle(sketch, "E48.2.10.0", {"center": v(159.36, -87.28) * mm, "radius": 2.31 * mm});
            skCircle(sketch, "E48.2.11.0", {"center": v(159.36, -99.98) * mm, "radius": 2.31 * mm});
            skCircle(sketch, "E48.2.12.0", {"center": v(159.36, -112.68) * mm, "radius": 2.31 * mm});
            skCircle(sketch, "E48.2.13.0", {"center": v(159.36, -125.38) * mm, "radius": 2.31 * mm});
            skCircle(sketch, "E48.3.0.0", {"center": v(172.06, 39.72) * mm, "radius": 2.31 * mm});
            skCircle(sketch, "E48.3.1.0", {"center": v(172.06, 27.02) * mm, "radius": 2.31 * mm});
            skCircle(sketch, "E48.3.2.0", {"center": v(172.06, 14.32) * mm, "radius": 2.31 * mm});
            skCircle(sketch, "E48.3.3.0", {"center": v(172.06, 1.62) * mm, "radius": 2.31 * mm});
            skCircle(sketch, "E48.3.4.0", {"center": v(172.06, -11.08) * mm, "radius": 2.31 * mm});
            skCircle(sketch, "E48.3.5.0", {"center": v(172.06, -23.78) * mm, "radius": 2.31 * mm});
            skCircle(sketch, "E48.3.6.0", {"center": v(172.06, -36.48) * mm, "radius": 2.31 * mm});
            skCircle(sketch, "E48.3.7.0", {"center": v(172.06, -49.18) * mm, "radius": 2.31 * mm});
            skCircle(sketch, "E48.3.8.0", {"center": v(172.06, -61.88) * mm, "radius": 2.31 * mm});
            skCircle(sketch, "E48.3.9.0", {"center": v(172.06, -74.58) * mm, "radius": 2.31 * mm});
            skCircle(sketch, "E48.3.10.0", {"center": v(172.06, -87.28) * mm, "radius": 2.31 * mm});
            skCircle(sketch, "E48.3.11.0", {"center": v(172.06, -99.98) * mm, "radius": 2.31 * mm});
            skCircle(sketch, "E48.3.12.0", {"center": v(172.06, -112.68) * mm, "radius": 2.31 * mm});
            skCircle(sketch, "E48.3.13.0", {"center": v(172.06, -125.38) * mm, "radius": 2.31 * mm});
            skCircle(sketch, "E48.4.0.0", {"center": v(184.76, 39.72) * mm, "radius": 2.31 * mm});
            skCircle(sketch, "E48.4.1.0", {"center": v(184.76, 27.02) * mm, "radius": 2.31 * mm});
            skCircle(sketch, "E48.4.2.0", {"center": v(184.76, 14.32) * mm, "radius": 2.31 * mm});
            skCircle(sketch, "E48.4.3.0", {"center": v(184.76, 1.62) * mm, "radius": 2.31 * mm});
            skCircle(sketch, "E48.4.5.0", {"center": v(184.76, -23.78) * mm, "radius": 2.31 * mm});
            skCircle(sketch, "E48.4.6.0", {"center": v(184.76, -36.48) * mm, "radius": 2.31 * mm});
            skCircle(sketch, "E48.4.7.0", {"center": v(184.76, -49.18) * mm, "radius": 2.31 * mm});
            skCircle(sketch, "E48.4.8.0", {"center": v(184.76, -61.88) * mm, "radius": 2.31 * mm});
            skCircle(sketch, "E48.4.10.0", {"center": v(184.76, -87.28) * mm, "radius": 2.31 * mm});
            skCircle(sketch, "E48.4.11.0", {"center": v(184.76, -99.98) * mm, "radius": 2.31 * mm});
            skCircle(sketch, "E48.4.12.0", {"center": v(184.76, -112.68) * mm, "radius": 2.31 * mm});
            skCircle(sketch, "E48.4.13.0", {"center": v(184.76, -125.38) * mm, "radius": 2.31 * mm});
            skCircle(sketch, "E48.5.0.0", {"center": v(197.46, 39.72) * mm, "radius": 2.31 * mm});
            skCircle(sketch, "E48.5.1.0", {"center": v(197.46, 27.02) * mm, "radius": 2.31 * mm});
            skCircle(sketch, "E48.5.2.0", {"center": v(197.46, 14.32) * mm, "radius": 2.31 * mm});
            skCircle(sketch, "E48.5.3.0", {"center": v(197.46, 1.62) * mm, "radius": 2.31 * mm});
            skCircle(sketch, "E48.5.4.0", {"center": v(197.46, -11.08) * mm, "radius": 2.31 * mm});
            skCircle(sketch, "E48.5.9.0", {"center": v(197.46, -74.58) * mm, "radius": 2.31 * mm});
            skCircle(sketch, "E48.5.10.0", {"center": v(197.46, -87.28) * mm, "radius": 2.31 * mm});
            skCircle(sketch, "E48.5.11.0", {"center": v(197.46, -99.98) * mm, "radius": 2.31 * mm});
            skCircle(sketch, "E48.5.12.0", {"center": v(197.46, -112.68) * mm, "radius": 2.31 * mm});
            skCircle(sketch, "E48.5.13.0", {"center": v(197.46, -125.38) * mm, "radius": 2.31 * mm});
            skCircle(sketch, "E48.6.0.0", {"center": v(210.16, 39.72) * mm, "radius": 2.31 * mm});
            skCircle(sketch, "E48.6.1.0", {"center": v(210.16, 27.02) * mm, "radius": 2.31 * mm});
            skCircle(sketch, "E48.6.2.0", {"center": v(210.16, 14.32) * mm, "radius": 2.31 * mm});
            skCircle(sketch, "E48.6.3.0", {"center": v(210.16, 1.62) * mm, "radius": 2.31 * mm});
            skCircle(sketch, "E48.6.4.0", {"center": v(210.16, -11.08) * mm, "radius": 2.31 * mm});
            skCircle(sketch, "E48.6.9.0", {"center": v(210.16, -74.58) * mm, "radius": 2.31 * mm});
            skCircle(sketch, "E48.6.10.0", {"center": v(210.16, -87.28) * mm, "radius": 2.31 * mm});
            skCircle(sketch, "E48.6.11.0", {"center": v(210.16, -99.98) * mm, "radius": 2.31 * mm});
            skCircle(sketch, "E48.6.12.0", {"center": v(210.16, -112.68) * mm, "radius": 2.31 * mm});
            skCircle(sketch, "E48.6.13.0", {"center": v(210.16, -125.38) * mm, "radius": 2.31 * mm});
            skCircle(sketch, "E48.7.0.0", {"center": v(222.86, 39.72) * mm, "radius": 2.31 * mm});
            skCircle(sketch, "E48.7.1.0", {"center": v(222.86, 27.02) * mm, "radius": 2.31 * mm});
            skCircle(sketch, "E48.7.2.0", {"center": v(222.86, 14.32) * mm, "radius": 2.31 * mm});
            skCircle(sketch, "E48.7.3.0", {"center": v(222.86, 1.62) * mm, "radius": 2.31 * mm});
            skCircle(sketch, "E48.7.4.0", {"center": v(222.86, -11.08) * mm, "radius": 2.31 * mm});
            skCircle(sketch, "E48.7.9.0", {"center": v(222.86, -74.58) * mm, "radius": 2.31 * mm});
            skCircle(sketch, "E48.7.10.0", {"center": v(222.86, -87.28) * mm, "radius": 2.31 * mm});
            skCircle(sketch, "E48.7.11.0", {"center": v(222.86, -99.98) * mm, "radius": 2.31 * mm});
            skCircle(sketch, "E48.7.12.0", {"center": v(222.86, -112.68) * mm, "radius": 2.31 * mm});
            skCircle(sketch, "E48.7.13.0", {"center": v(222.86, -125.38) * mm, "radius": 2.31 * mm});
            skCircle(sketch, "E48.8.0.0", {"center": v(235.56, 39.72) * mm, "radius": 2.31 * mm});
            skCircle(sketch, "E48.8.1.0", {"center": v(235.56, 27.02) * mm, "radius": 2.31 * mm});
            skCircle(sketch, "E48.8.2.0", {"center": v(235.56, 14.32) * mm, "radius": 2.31 * mm});
            skCircle(sketch, "E48.8.3.0", {"center": v(235.56, 1.62) * mm, "radius": 2.31 * mm});
            skCircle(sketch, "E48.8.4.0", {"center": v(235.56, -11.08) * mm, "radius": 2.31 * mm});
            skCircle(sketch, "E48.8.9.0", {"center": v(235.56, -74.58) * mm, "radius": 2.31 * mm});
            skCircle(sketch, "E48.8.10.0", {"center": v(235.56, -87.28) * mm, "radius": 2.31 * mm});
            skCircle(sketch, "E48.8.11.0", {"center": v(235.56, -99.98) * mm, "radius": 2.31 * mm});
            skCircle(sketch, "E48.8.12.0", {"center": v(235.56, -112.68) * mm, "radius": 2.31 * mm});
            skCircle(sketch, "E48.8.13.0", {"center": v(235.56, -125.38) * mm, "radius": 2.31 * mm});
            skCircle(sketch, "E48.9.0.0", {"center": v(248.26, 39.72) * mm, "radius": 2.31 * mm});
            skCircle(sketch, "E48.9.1.0", {"center": v(248.26, 27.02) * mm, "radius": 2.31 * mm});
            skCircle(sketch, "E48.9.2.0", {"center": v(248.26, 14.32) * mm, "radius": 2.31 * mm});
            skCircle(sketch, "E48.9.3.0", {"center": v(248.26, 1.62) * mm, "radius": 2.31 * mm});
            skCircle(sketch, "E48.9.4.0", {"center": v(248.26, -11.08) * mm, "radius": 2.31 * mm});
            skCircle(sketch, "E48.9.9.0", {"center": v(248.26, -74.58) * mm, "radius": 2.31 * mm});
            skCircle(sketch, "E48.9.10.0", {"center": v(248.26, -87.28) * mm, "radius": 2.31 * mm});
            skCircle(sketch, "E48.9.11.0", {"center": v(248.26, -99.98) * mm, "radius": 2.31 * mm});
            skCircle(sketch, "E48.9.12.0", {"center": v(248.26, -112.68) * mm, "radius": 2.31 * mm});
            skCircle(sketch, "E48.9.13.0", {"center": v(248.26, -125.38) * mm, "radius": 2.31 * mm});
            skCircle(sketch, "E48.10.0.0", {"center": v(260.96, 39.72) * mm, "radius": 2.31 * mm});
            skCircle(sketch, "E48.10.1.0", {"center": v(260.96, 27.02) * mm, "radius": 2.31 * mm});
            skCircle(sketch, "E48.10.2.0", {"center": v(260.96, 14.32) * mm, "radius": 2.31 * mm});
            skCircle(sketch, "E48.10.3.0", {"center": v(260.96, 1.62) * mm, "radius": 2.31 * mm});
            skCircle(sketch, "E48.10.4.0", {"center": v(260.96, -11.08) * mm, "radius": 2.31 * mm});
            skCircle(sketch, "E48.10.9.0", {"center": v(260.96, -74.58) * mm, "radius": 2.31 * mm});
            skCircle(sketch, "E48.10.10.0", {"center": v(260.96, -87.28) * mm, "radius": 2.31 * mm});
            skCircle(sketch, "E48.10.11.0", {"center": v(260.96, -99.98) * mm, "radius": 2.31 * mm});
            skCircle(sketch, "E48.10.12.0", {"center": v(260.96, -112.68) * mm, "radius": 2.31 * mm});
            skCircle(sketch, "E48.10.13.0", {"center": v(260.96, -125.38) * mm, "radius": 2.31 * mm});
            skCircle(sketch, "E48.11.0.0", {"center": v(273.66, 39.72) * mm, "radius": 2.31 * mm});
            skCircle(sketch, "E48.11.1.0", {"center": v(273.66, 27.02) * mm, "radius": 2.31 * mm});
            skCircle(sketch, "E48.11.2.0", {"center": v(273.66, 14.32) * mm, "radius": 2.31 * mm});
            skCircle(sketch, "E48.11.3.0", {"center": v(273.66, 1.62) * mm, "radius": 2.31 * mm});
            skCircle(sketch, "E48.11.4.0", {"center": v(273.66, -11.08) * mm, "radius": 2.31 * mm});
            skCircle(sketch, "E48.11.9.0", {"center": v(273.66, -74.58) * mm, "radius": 2.31 * mm});
            skCircle(sketch, "E48.11.10.0", {"center": v(273.66, -87.28) * mm, "radius": 2.31 * mm});
            skCircle(sketch, "E48.11.11.0", {"center": v(273.66, -99.98) * mm, "radius": 2.31 * mm});
            skCircle(sketch, "E48.11.12.0", {"center": v(273.66, -112.68) * mm, "radius": 2.31 * mm});
            skCircle(sketch, "E48.11.13.0", {"center": v(273.66, -125.38) * mm, "radius": 2.31 * mm});
            skCircle(sketch, "E48.12.0.0", {"center": v(286.36, 39.72) * mm, "radius": 2.31 * mm});
            skCircle(sketch, "E48.12.1.0", {"center": v(286.36, 27.02) * mm, "radius": 2.31 * mm});
            skCircle(sketch, "E48.12.2.0", {"center": v(286.36, 14.32) * mm, "radius": 2.31 * mm});
            skCircle(sketch, "E48.12.3.0", {"center": v(286.36, 1.62) * mm, "radius": 2.31 * mm});
            skCircle(sketch, "E48.12.4.0", {"center": v(286.36, -11.08) * mm, "radius": 2.31 * mm});
            skCircle(sketch, "E48.12.9.0", {"center": v(286.36, -74.58) * mm, "radius": 2.31 * mm});
            skCircle(sketch, "E48.12.10.0", {"center": v(286.36, -87.28) * mm, "radius": 2.31 * mm});
            skCircle(sketch, "E48.12.11.0", {"center": v(286.36, -99.98) * mm, "radius": 2.31 * mm});
            skCircle(sketch, "E48.12.12.0", {"center": v(286.36, -112.68) * mm, "radius": 2.31 * mm});
            skCircle(sketch, "E48.12.13.0", {"center": v(286.36, -125.38) * mm, "radius": 2.31 * mm});
            skCircle(sketch, "E48.13.0.0", {"center": v(299.06, 39.72) * mm, "radius": 2.31 * mm});
            skCircle(sketch, "E48.13.1.0", {"center": v(299.06, 27.02) * mm, "radius": 2.31 * mm});
            skCircle(sketch, "E48.13.2.0", {"center": v(299.06, 14.32) * mm, "radius": 2.31 * mm});
            skCircle(sketch, "E48.13.3.0", {"center": v(299.06, 1.62) * mm, "radius": 2.31 * mm});
            skCircle(sketch, "E48.13.4.0", {"center": v(299.06, -11.08) * mm, "radius": 2.31 * mm});
            skCircle(sketch, "E48.13.9.0", {"center": v(299.06, -74.58) * mm, "radius": 2.31 * mm});
            skCircle(sketch, "E48.13.10.0", {"center": v(299.06, -87.28) * mm, "radius": 2.31 * mm});
            skCircle(sketch, "E48.13.11.0", {"center": v(299.06, -99.98) * mm, "radius": 2.31 * mm});
            skCircle(sketch, "E48.13.12.0", {"center": v(299.06, -112.68) * mm, "radius": 2.31 * mm});
            skCircle(sketch, "E48.13.13.0", {"center": v(299.06, -125.38) * mm, "radius": 2.31 * mm});
            skCircle(sketch, "E48.14.0.0", {"center": v(311.76, 39.72) * mm, "radius": 2.31 * mm});
            skCircle(sketch, "E48.14.1.0", {"center": v(311.76, 27.02) * mm, "radius": 2.31 * mm});
            skCircle(sketch, "E48.14.2.0", {"center": v(311.76, 14.32) * mm, "radius": 2.31 * mm});
            skCircle(sketch, "E48.14.3.0", {"center": v(311.76, 1.62) * mm, "radius": 2.31 * mm});
            skCircle(sketch, "E48.14.4.0", {"center": v(311.76, -11.08) * mm, "radius": 2.31 * mm});
            skCircle(sketch, "E48.14.9.0", {"center": v(311.76, -74.58) * mm, "radius": 2.31 * mm});
            skCircle(sketch, "E48.14.10.0", {"center": v(311.76, -87.28) * mm, "radius": 2.31 * mm});
            skCircle(sketch, "E48.14.11.0", {"center": v(311.76, -99.98) * mm, "radius": 2.31 * mm});
            skCircle(sketch, "E48.14.12.0", {"center": v(311.76, -112.68) * mm, "radius": 2.31 * mm});
            skCircle(sketch, "E48.14.13.0", {"center": v(311.76, -125.38) * mm, "radius": 2.31 * mm});
            skCircle(sketch, "E48.15.0.0", {"center": v(324.46, 39.72) * mm, "radius": 2.31 * mm});
            skCircle(sketch, "E48.15.1.0", {"center": v(324.46, 27.02) * mm, "radius": 2.31 * mm});
            skCircle(sketch, "E48.15.2.0", {"center": v(324.46, 14.32) * mm, "radius": 2.31 * mm});
            skCircle(sketch, "E48.15.3.0", {"center": v(324.46, 1.62) * mm, "radius": 2.31 * mm});
            skCircle(sketch, "E48.15.5.0", {"center": v(324.46, -23.78) * mm, "radius": 2.31 * mm});
            skCircle(sketch, "E48.15.6.0", {"center": v(324.46, -36.48) * mm, "radius": 2.31 * mm});
            skCircle(sketch, "E48.15.7.0", {"center": v(324.46, -49.18) * mm, "radius": 2.31 * mm});
            skCircle(sketch, "E48.15.8.0", {"center": v(324.46, -61.88) * mm, "radius": 2.31 * mm});
            skCircle(sketch, "E48.15.10.0", {"center": v(324.46, -87.28) * mm, "radius": 2.31 * mm});
            skCircle(sketch, "E48.15.11.0", {"center": v(324.46, -99.98) * mm, "radius": 2.31 * mm});
            skCircle(sketch, "E48.15.12.0", {"center": v(324.46, -112.68) * mm, "radius": 2.31 * mm});
            skCircle(sketch, "E48.15.13.0", {"center": v(324.46, -125.38) * mm, "radius": 2.31 * mm});
            skCircle(sketch, "E48.16.0.0", {"center": v(337.16, 39.72) * mm, "radius": 2.31 * mm});
            skCircle(sketch, "E48.16.1.0", {"center": v(337.16, 27.02) * mm, "radius": 2.31 * mm});
            skCircle(sketch, "E48.16.2.0", {"center": v(337.16, 14.32) * mm, "radius": 2.31 * mm});
            skCircle(sketch, "E48.16.3.0", {"center": v(337.16, 1.62) * mm, "radius": 2.31 * mm});
            skCircle(sketch, "E48.16.4.0", {"center": v(337.16, -11.08) * mm, "radius": 2.31 * mm});
            skCircle(sketch, "E48.16.5.0", {"center": v(337.16, -23.78) * mm, "radius": 2.31 * mm});
            skCircle(sketch, "E48.16.6.0", {"center": v(337.16, -36.48) * mm, "radius": 2.31 * mm});
            skCircle(sketch, "E48.16.7.0", {"center": v(337.16, -49.18) * mm, "radius": 2.31 * mm});
            skCircle(sketch, "E48.16.8.0", {"center": v(337.16, -61.88) * mm, "radius": 2.31 * mm});
            skCircle(sketch, "E48.16.9.0", {"center": v(337.16, -74.58) * mm, "radius": 2.31 * mm});
            skCircle(sketch, "E48.16.10.0", {"center": v(337.16, -87.28) * mm, "radius": 2.31 * mm});
            skCircle(sketch, "E48.16.11.0", {"center": v(337.16, -99.98) * mm, "radius": 2.31 * mm});
            skCircle(sketch, "E48.16.12.0", {"center": v(337.16, -112.68) * mm, "radius": 2.31 * mm});
            skCircle(sketch, "E48.16.13.0", {"center": v(337.16, -125.38) * mm, "radius": 2.31 * mm});
            skCircle(sketch, "E48.17.0.0", {"center": v(349.86, 39.72) * mm, "radius": 2.31 * mm});
            skCircle(sketch, "E48.17.1.0", {"center": v(349.86, 27.02) * mm, "radius": 2.31 * mm});
            skCircle(sketch, "E48.17.2.0", {"center": v(349.86, 14.32) * mm, "radius": 2.31 * mm});
            skCircle(sketch, "E48.17.3.0", {"center": v(349.86, 1.62) * mm, "radius": 2.31 * mm});
            skCircle(sketch, "E48.17.4.0", {"center": v(349.86, -11.08) * mm, "radius": 2.31 * mm});
            skCircle(sketch, "E48.17.5.0", {"center": v(349.86, -23.78) * mm, "radius": 2.31 * mm});
            skCircle(sketch, "E48.17.6.0", {"center": v(349.86, -36.48) * mm, "radius": 2.31 * mm});
            skCircle(sketch, "E48.17.7.0", {"center": v(349.86, -49.18) * mm, "radius": 2.31 * mm});
            skCircle(sketch, "E48.17.8.0", {"center": v(349.86, -61.88) * mm, "radius": 2.31 * mm});
            skCircle(sketch, "E48.17.9.0", {"center": v(349.86, -74.58) * mm, "radius": 2.31 * mm});
            skCircle(sketch, "E48.17.10.0", {"center": v(349.86, -87.28) * mm, "radius": 2.31 * mm});
            skCircle(sketch, "E48.17.11.0", {"center": v(349.86, -99.98) * mm, "radius": 2.31 * mm});
            skCircle(sketch, "E48.17.12.0", {"center": v(349.86, -112.68) * mm, "radius": 2.31 * mm});
            skCircle(sketch, "E48.17.13.0", {"center": v(349.86, -125.38) * mm, "radius": 2.31 * mm});
            skCircle(sketch, "E48.18.0.0", {"center": v(362.56, 39.72) * mm, "radius": 2.31 * mm});
            skCircle(sketch, "E48.18.1.0", {"center": v(362.56, 27.02) * mm, "radius": 2.31 * mm});
            skCircle(sketch, "E48.18.2.0", {"center": v(362.56, 14.32) * mm, "radius": 2.31 * mm});
            skCircle(sketch, "E48.18.3.0", {"center": v(362.56, 1.62) * mm, "radius": 2.31 * mm});
            skCircle(sketch, "E48.18.4.0", {"center": v(362.56, -11.08) * mm, "radius": 2.31 * mm});
            skCircle(sketch, "E48.18.5.0", {"center": v(362.56, -23.78) * mm, "radius": 2.31 * mm});
            skCircle(sketch, "E48.18.6.0", {"center": v(362.56, -36.48) * mm, "radius": 2.31 * mm});
            skCircle(sketch, "E48.18.7.0", {"center": v(362.56, -49.18) * mm, "radius": 2.31 * mm});
            skCircle(sketch, "E48.18.8.0", {"center": v(362.56, -61.88) * mm, "radius": 2.31 * mm});
            skCircle(sketch, "E48.18.9.0", {"center": v(362.56, -74.58) * mm, "radius": 2.31 * mm});
            skCircle(sketch, "E48.18.10.0", {"center": v(362.56, -87.28) * mm, "radius": 2.31 * mm});
            skCircle(sketch, "E48.18.11.0", {"center": v(362.56, -99.98) * mm, "radius": 2.31 * mm});
            skCircle(sketch, "E48.18.12.0", {"center": v(362.56, -112.68) * mm, "radius": 2.31 * mm});
            skCircle(sketch, "E48.18.13.0", {"center": v(362.56, -125.38) * mm, "radius": 2.31 * mm});
            skLineSegment(sketch, "E48.direction1", {"start": v(133.96, 39.72) * mm, "end": v(146.66, 39.72) * mm, "construction": true});
            skLineSegment(sketch, "E48.direction2", {"start": v(133.96, 39.72) * mm, "end": v(133.96, 27.02) * mm, "construction": true});
            skCircle(sketch, "E49.0.19.0", {"center": v(375.26, 39.72) * mm, "radius": 2.31 * mm});
            skCircle(sketch, "E49.0.19.1", {"center": v(375.26, 27.02) * mm, "radius": 2.31 * mm});
            skCircle(sketch, "E49.0.19.2", {"center": v(375.26, 14.32) * mm, "radius": 2.31 * mm});
            skCircle(sketch, "E49.0.19.3", {"center": v(375.26, 1.62) * mm, "radius": 2.31 * mm});
            skCircle(sketch, "E49.0.19.4", {"center": v(375.26, -11.08) * mm, "radius": 2.31 * mm});
            skCircle(sketch, "E49.0.19.5", {"center": v(375.26, -23.78) * mm, "radius": 2.31 * mm});
            skCircle(sketch, "E49.0.19.6", {"center": v(375.26, -36.48) * mm, "radius": 2.31 * mm});
            skCircle(sketch, "E49.0.19.7", {"center": v(375.26, -49.18) * mm, "radius": 2.31 * mm});
            skCircle(sketch, "E49.0.19.8", {"center": v(375.26, -61.88) * mm, "radius": 2.31 * mm});
            skCircle(sketch, "E49.0.19.9", {"center": v(375.26, -74.58) * mm, "radius": 2.31 * mm});
            skCircle(sketch, "E49.0.19.10", {"center": v(375.26, -87.28) * mm, "radius": 2.31 * mm});
            skCircle(sketch, "E49.0.19.11", {"center": v(375.26, -99.98) * mm, "radius": 2.31 * mm});
            skCircle(sketch, "E49.0.19.12", {"center": v(375.26, -112.68) * mm, "radius": 2.31 * mm});
            skCircle(sketch, "E49.0.19.13", {"center": v(375.26, -125.38) * mm, "radius": 2.31 * mm});
            skCircle(sketch, "E50", {"center": v(140.3, 33.37) * mm, "radius": 2.31 * mm});
            skCircle(sketch, "E51.0.1.0", {"center": v(140.3, 20.67) * mm, "radius": 2.31 * mm});
            skCircle(sketch, "E51.0.2.0", {"center": v(140.3, 7.97) * mm, "radius": 2.31 * mm});
            skCircle(sketch, "E51.0.3.0", {"center": v(140.3, -4.73) * mm, "radius": 2.31 * mm});
            skCircle(sketch, "E51.0.4.0", {"center": v(140.3, -17.43) * mm, "radius": 2.31 * mm});
            skCircle(sketch, "E51.0.5.0", {"center": v(140.3, -30.13) * mm, "radius": 2.31 * mm});
            skCircle(sketch, "E51.0.6.0", {"center": v(140.3, -42.83) * mm, "radius": 2.31 * mm});
            skCircle(sketch, "E51.0.7.0", {"center": v(140.3, -55.53) * mm, "radius": 2.31 * mm});
            skCircle(sketch, "E51.0.8.0", {"center": v(140.3, -68.23) * mm, "radius": 2.31 * mm});
            skCircle(sketch, "E51.0.9.0", {"center": v(140.3, -80.93) * mm, "radius": 2.31 * mm});
            skCircle(sketch, "E51.0.10.0", {"center": v(140.3, -93.63) * mm, "radius": 2.31 * mm});
            skCircle(sketch, "E51.0.11.0", {"center": v(140.3, -106.33) * mm, "radius": 2.31 * mm});
            skCircle(sketch, "E51.0.12.0", {"center": v(140.3, -119.03) * mm, "radius": 2.31 * mm});
            skCircle(sketch, "E51.1.0.0", {"center": v(153, 33.37) * mm, "radius": 2.31 * mm});
            skCircle(sketch, "E51.1.1.0", {"center": v(153, 20.67) * mm, "radius": 2.31 * mm});
            skCircle(sketch, "E51.1.2.0", {"center": v(153, 7.97) * mm, "radius": 2.31 * mm});
            skCircle(sketch, "E51.1.3.0", {"center": v(153, -4.73) * mm, "radius": 2.31 * mm});
            skCircle(sketch, "E51.1.4.0", {"center": v(153, -17.43) * mm, "radius": 2.31 * mm});
            skCircle(sketch, "E51.1.5.0", {"center": v(153, -30.13) * mm, "radius": 2.31 * mm});
            skCircle(sketch, "E51.1.6.0", {"center": v(153, -42.83) * mm, "radius": 2.31 * mm});
            skCircle(sketch, "E51.1.7.0", {"center": v(153, -55.53) * mm, "radius": 2.31 * mm});
            skCircle(sketch, "E51.1.8.0", {"center": v(153, -68.23) * mm, "radius": 2.31 * mm});
            skCircle(sketch, "E51.1.9.0", {"center": v(153, -80.93) * mm, "radius": 2.31 * mm});
            skCircle(sketch, "E51.1.10.0", {"center": v(153, -93.63) * mm, "radius": 2.31 * mm});
            skCircle(sketch, "E51.1.11.0", {"center": v(153, -106.33) * mm, "radius": 2.31 * mm});
            skCircle(sketch, "E51.1.12.0", {"center": v(153, -119.03) * mm, "radius": 2.31 * mm});
            skCircle(sketch, "E51.2.0.0", {"center": v(165.7, 33.37) * mm, "radius": 2.31 * mm});
            skCircle(sketch, "E51.2.1.0", {"center": v(165.7, 20.67) * mm, "radius": 2.31 * mm});
            skCircle(sketch, "E51.2.2.0", {"center": v(165.7, 7.97) * mm, "radius": 2.31 * mm});
            skCircle(sketch, "E51.2.3.0", {"center": v(165.7, -4.73) * mm, "radius": 2.31 * mm});
            skCircle(sketch, "E51.2.4.0", {"center": v(165.7, -17.43) * mm, "radius": 2.31 * mm});
            skCircle(sketch, "E51.2.5.0", {"center": v(165.7, -30.13) * mm, "radius": 2.31 * mm});
            skCircle(sketch, "E51.2.6.0", {"center": v(165.7, -42.83) * mm, "radius": 2.31 * mm});
            skCircle(sketch, "E51.2.7.0", {"center": v(165.7, -55.53) * mm, "radius": 2.31 * mm});
            skCircle(sketch, "E51.2.8.0", {"center": v(165.7, -68.23) * mm, "radius": 2.31 * mm});
            skCircle(sketch, "E51.2.9.0", {"center": v(165.7, -80.93) * mm, "radius": 2.31 * mm});
            skCircle(sketch, "E51.2.10.0", {"center": v(165.7, -93.63) * mm, "radius": 2.31 * mm});
            skCircle(sketch, "E51.2.11.0", {"center": v(165.7, -106.33) * mm, "radius": 2.31 * mm});
            skCircle(sketch, "E51.2.12.0", {"center": v(165.7, -119.03) * mm, "radius": 2.31 * mm});
            skCircle(sketch, "E51.3.0.0", {"center": v(178.4, 33.37) * mm, "radius": 2.31 * mm});
            skCircle(sketch, "E51.3.1.0", {"center": v(178.4, 20.67) * mm, "radius": 2.31 * mm});
            skCircle(sketch, "E51.3.2.0", {"center": v(178.4, 7.97) * mm, "radius": 2.31 * mm});
            skCircle(sketch, "E51.3.3.0", {"center": v(178.4, -4.73) * mm, "radius": 2.31 * mm});
            skCircle(sketch, "E51.3.4.0", {"center": v(178.4, -17.43) * mm, "radius": 2.31 * mm});
            skCircle(sketch, "E51.3.5.0", {"center": v(178.4, -30.13) * mm, "radius": 2.31 * mm});
            skCircle(sketch, "E51.3.6.0", {"center": v(178.4, -42.83) * mm, "radius": 2.31 * mm});
            skCircle(sketch, "E51.3.7.0", {"center": v(178.4, -55.53) * mm, "radius": 2.31 * mm});
            skCircle(sketch, "E51.3.8.0", {"center": v(178.4, -68.23) * mm, "radius": 2.31 * mm});
            skCircle(sketch, "E51.3.9.0", {"center": v(178.4, -80.93) * mm, "radius": 2.31 * mm});
            skCircle(sketch, "E51.3.10.0", {"center": v(178.4, -93.63) * mm, "radius": 2.31 * mm});
            skCircle(sketch, "E51.3.11.0", {"center": v(178.4, -106.33) * mm, "radius": 2.31 * mm});
            skCircle(sketch, "E51.3.12.0", {"center": v(178.4, -119.03) * mm, "radius": 2.31 * mm});
            skCircle(sketch, "E51.4.0.0", {"center": v(191.1, 33.37) * mm, "radius": 2.31 * mm});
            skCircle(sketch, "E51.4.1.0", {"center": v(191.1, 20.67) * mm, "radius": 2.31 * mm});
            skCircle(sketch, "E51.4.2.0", {"center": v(191.1, 7.97) * mm, "radius": 2.31 * mm});
            skCircle(sketch, "E51.4.3.0", {"center": v(191.1, -4.73) * mm, "radius": 2.31 * mm});
            skCircle(sketch, "E51.4.9.0", {"center": v(191.1, -80.93) * mm, "radius": 2.31 * mm});
            skCircle(sketch, "E51.4.10.0", {"center": v(191.1, -93.63) * mm, "radius": 2.31 * mm});
            skCircle(sketch, "E51.4.11.0", {"center": v(191.1, -106.33) * mm, "radius": 2.31 * mm});
            skCircle(sketch, "E51.4.12.0", {"center": v(191.1, -119.03) * mm, "radius": 2.31 * mm});
            skCircle(sketch, "E51.5.0.0", {"center": v(203.8, 33.37) * mm, "radius": 2.31 * mm});
            skCircle(sketch, "E51.5.1.0", {"center": v(203.8, 20.67) * mm, "radius": 2.31 * mm});
            skCircle(sketch, "E51.5.2.0", {"center": v(203.8, 7.97) * mm, "radius": 2.31 * mm});
            skCircle(sketch, "E51.5.3.0", {"center": v(203.8, -4.73) * mm, "radius": 2.31 * mm});
            skCircle(sketch, "E51.5.9.0", {"center": v(203.8, -80.93) * mm, "radius": 2.31 * mm});
            skCircle(sketch, "E51.5.10.0", {"center": v(203.8, -93.63) * mm, "radius": 2.31 * mm});
            skCircle(sketch, "E51.5.11.0", {"center": v(203.8, -106.33) * mm, "radius": 2.31 * mm});
            skCircle(sketch, "E51.5.12.0", {"center": v(203.8, -119.03) * mm, "radius": 2.31 * mm});
            skCircle(sketch, "E51.6.0.0", {"center": v(216.5, 33.37) * mm, "radius": 2.31 * mm});
            skCircle(sketch, "E51.6.1.0", {"center": v(216.5, 20.67) * mm, "radius": 2.31 * mm});
            skCircle(sketch, "E51.6.2.0", {"center": v(216.5, 7.97) * mm, "radius": 2.31 * mm});
            skCircle(sketch, "E51.6.3.0", {"center": v(216.5, -4.73) * mm, "radius": 2.31 * mm});
            skCircle(sketch, "E51.6.9.0", {"center": v(216.5, -80.93) * mm, "radius": 2.31 * mm});
            skCircle(sketch, "E51.6.10.0", {"center": v(216.5, -93.63) * mm, "radius": 2.31 * mm});
            skCircle(sketch, "E51.6.11.0", {"center": v(216.5, -106.33) * mm, "radius": 2.31 * mm});
            skCircle(sketch, "E51.6.12.0", {"center": v(216.5, -119.03) * mm, "radius": 2.31 * mm});
            skCircle(sketch, "E51.7.0.0", {"center": v(229.2, 33.37) * mm, "radius": 2.31 * mm});
            skCircle(sketch, "E51.7.1.0", {"center": v(229.2, 20.67) * mm, "radius": 2.31 * mm});
            skCircle(sketch, "E51.7.2.0", {"center": v(229.2, 7.97) * mm, "radius": 2.31 * mm});
            skCircle(sketch, "E51.7.3.0", {"center": v(229.2, -4.73) * mm, "radius": 2.31 * mm});
            skCircle(sketch, "E51.7.9.0", {"center": v(229.2, -80.93) * mm, "radius": 2.31 * mm});
            skCircle(sketch, "E51.7.10.0", {"center": v(229.2, -93.63) * mm, "radius": 2.31 * mm});
            skCircle(sketch, "E51.7.11.0", {"center": v(229.2, -106.33) * mm, "radius": 2.31 * mm});
            skCircle(sketch, "E51.7.12.0", {"center": v(229.2, -119.03) * mm, "radius": 2.31 * mm});
            skCircle(sketch, "E51.8.0.0", {"center": v(241.9, 33.37) * mm, "radius": 2.31 * mm});
            skCircle(sketch, "E51.8.1.0", {"center": v(241.9, 20.67) * mm, "radius": 2.31 * mm});
            skCircle(sketch, "E51.8.2.0", {"center": v(241.9, 7.97) * mm, "radius": 2.31 * mm});
            skCircle(sketch, "E51.8.3.0", {"center": v(241.9, -4.73) * mm, "radius": 2.31 * mm});
            skCircle(sketch, "E51.8.9.0", {"center": v(241.9, -80.93) * mm, "radius": 2.31 * mm});
            skCircle(sketch, "E51.8.10.0", {"center": v(241.9, -93.63) * mm, "radius": 2.31 * mm});
            skCircle(sketch, "E51.8.11.0", {"center": v(241.9, -106.33) * mm, "radius": 2.31 * mm});
            skCircle(sketch, "E51.8.12.0", {"center": v(241.9, -119.03) * mm, "radius": 2.31 * mm});
            skCircle(sketch, "E51.9.0.0", {"center": v(254.6, 33.37) * mm, "radius": 2.31 * mm});
            skCircle(sketch, "E51.9.1.0", {"center": v(254.6, 20.67) * mm, "radius": 2.31 * mm});
            skCircle(sketch, "E51.9.2.0", {"center": v(254.6, 7.97) * mm, "radius": 2.31 * mm});
            skCircle(sketch, "E51.9.3.0", {"center": v(254.6, -4.73) * mm, "radius": 2.31 * mm});
            skCircle(sketch, "E51.9.9.0", {"center": v(254.6, -80.93) * mm, "radius": 2.31 * mm});
            skCircle(sketch, "E51.9.10.0", {"center": v(254.6, -93.63) * mm, "radius": 2.31 * mm});
            skCircle(sketch, "E51.9.11.0", {"center": v(254.6, -106.33) * mm, "radius": 2.31 * mm});
            skCircle(sketch, "E51.9.12.0", {"center": v(254.6, -119.03) * mm, "radius": 2.31 * mm});
            skCircle(sketch, "E51.10.0.0", {"center": v(267.3, 33.37) * mm, "radius": 2.31 * mm});
            skCircle(sketch, "E51.10.1.0", {"center": v(267.3, 20.67) * mm, "radius": 2.31 * mm});
            skCircle(sketch, "E51.10.2.0", {"center": v(267.3, 7.97) * mm, "radius": 2.31 * mm});
            skCircle(sketch, "E51.10.3.0", {"center": v(267.3, -4.73) * mm, "radius": 2.31 * mm});
            skCircle(sketch, "E51.10.9.0", {"center": v(267.3, -80.93) * mm, "radius": 2.31 * mm});
            skCircle(sketch, "E51.10.10.0", {"center": v(267.3, -93.63) * mm, "radius": 2.31 * mm});
            skCircle(sketch, "E51.10.11.0", {"center": v(267.3, -106.33) * mm, "radius": 2.31 * mm});
            skCircle(sketch, "E51.10.12.0", {"center": v(267.3, -119.03) * mm, "radius": 2.31 * mm});
            skCircle(sketch, "E51.11.0.0", {"center": v(280, 33.37) * mm, "radius": 2.31 * mm});
            skCircle(sketch, "E51.11.1.0", {"center": v(280, 20.67) * mm, "radius": 2.31 * mm});
            skCircle(sketch, "E51.11.2.0", {"center": v(280, 7.97) * mm, "radius": 2.31 * mm});
            skCircle(sketch, "E51.11.3.0", {"center": v(280, -4.73) * mm, "radius": 2.31 * mm});
            skCircle(sketch, "E51.11.9.0", {"center": v(280, -80.93) * mm, "radius": 2.31 * mm});
            skCircle(sketch, "E51.11.10.0", {"center": v(280, -93.63) * mm, "radius": 2.31 * mm});
            skCircle(sketch, "E51.11.11.0", {"center": v(280, -106.33) * mm, "radius": 2.31 * mm});
            skCircle(sketch, "E51.11.12.0", {"center": v(280, -119.03) * mm, "radius": 2.31 * mm});
            skCircle(sketch, "E51.12.0.0", {"center": v(292.7, 33.37) * mm, "radius": 2.31 * mm});
            skCircle(sketch, "E51.12.1.0", {"center": v(292.7, 20.67) * mm, "radius": 2.31 * mm});
            skCircle(sketch, "E51.12.2.0", {"center": v(292.7, 7.97) * mm, "radius": 2.31 * mm});
            skCircle(sketch, "E51.12.3.0", {"center": v(292.7, -4.73) * mm, "radius": 2.31 * mm});
            skCircle(sketch, "E51.12.9.0", {"center": v(292.7, -80.93) * mm, "radius": 2.31 * mm});
            skCircle(sketch, "E51.12.10.0", {"center": v(292.7, -93.63) * mm, "radius": 2.31 * mm});
            skCircle(sketch, "E51.12.11.0", {"center": v(292.7, -106.33) * mm, "radius": 2.31 * mm});
            skCircle(sketch, "E51.12.12.0", {"center": v(292.7, -119.03) * mm, "radius": 2.31 * mm});
            skCircle(sketch, "E51.13.0.0", {"center": v(305.4, 33.37) * mm, "radius": 2.31 * mm});
            skCircle(sketch, "E51.13.1.0", {"center": v(305.4, 20.67) * mm, "radius": 2.31 * mm});
            skCircle(sketch, "E51.13.2.0", {"center": v(305.4, 7.97) * mm, "radius": 2.31 * mm});
            skCircle(sketch, "E51.13.3.0", {"center": v(305.4, -4.73) * mm, "radius": 2.31 * mm});
            skCircle(sketch, "E51.13.9.0", {"center": v(305.4, -80.93) * mm, "radius": 2.31 * mm});
            skCircle(sketch, "E51.13.10.0", {"center": v(305.4, -93.63) * mm, "radius": 2.31 * mm});
            skCircle(sketch, "E51.13.11.0", {"center": v(305.4, -106.33) * mm, "radius": 2.31 * mm});
            skCircle(sketch, "E51.13.12.0", {"center": v(305.4, -119.03) * mm, "radius": 2.31 * mm});
            skCircle(sketch, "E51.14.0.0", {"center": v(318.1, 33.37) * mm, "radius": 2.31 * mm});
            skCircle(sketch, "E51.14.1.0", {"center": v(318.1, 20.67) * mm, "radius": 2.31 * mm});
            skCircle(sketch, "E51.14.2.0", {"center": v(318.1, 7.97) * mm, "radius": 2.31 * mm});
            skCircle(sketch, "E51.14.3.0", {"center": v(318.1, -4.73) * mm, "radius": 2.31 * mm});
            skCircle(sketch, "E51.14.9.0", {"center": v(318.1, -80.93) * mm, "radius": 2.31 * mm});
            skCircle(sketch, "E51.14.10.0", {"center": v(318.1, -93.63) * mm, "radius": 2.31 * mm});
            skCircle(sketch, "E51.14.11.0", {"center": v(318.1, -106.33) * mm, "radius": 2.31 * mm});
            skCircle(sketch, "E51.14.12.0", {"center": v(318.1, -119.03) * mm, "radius": 2.31 * mm});
            skCircle(sketch, "E51.15.0.0", {"center": v(330.8, 33.37) * mm, "radius": 2.31 * mm});
            skCircle(sketch, "E51.15.1.0", {"center": v(330.8, 20.67) * mm, "radius": 2.31 * mm});
            skCircle(sketch, "E51.15.2.0", {"center": v(330.8, 7.97) * mm, "radius": 2.31 * mm});
            skCircle(sketch, "E51.15.3.0", {"center": v(330.8, -4.73) * mm, "radius": 2.31 * mm});
            skCircle(sketch, "E51.15.4.0", {"center": v(330.8, -17.43) * mm, "radius": 2.31 * mm});
            skCircle(sketch, "E51.15.5.0", {"center": v(330.8, -30.13) * mm, "radius": 2.31 * mm});
            skCircle(sketch, "E51.15.6.0", {"center": v(330.8, -42.83) * mm, "radius": 2.31 * mm});
            skCircle(sketch, "E51.15.7.0", {"center": v(330.8, -55.53) * mm, "radius": 2.31 * mm});
            skCircle(sketch, "E51.15.8.0", {"center": v(330.8, -68.23) * mm, "radius": 2.31 * mm});
            skCircle(sketch, "E51.15.9.0", {"center": v(330.8, -80.93) * mm, "radius": 2.31 * mm});
            skCircle(sketch, "E51.15.10.0", {"center": v(330.8, -93.63) * mm, "radius": 2.31 * mm});
            skCircle(sketch, "E51.15.11.0", {"center": v(330.8, -106.33) * mm, "radius": 2.31 * mm});
            skCircle(sketch, "E51.15.12.0", {"center": v(330.8, -119.03) * mm, "radius": 2.31 * mm});
            skCircle(sketch, "E51.16.0.0", {"center": v(343.5, 33.37) * mm, "radius": 2.31 * mm});
            skCircle(sketch, "E51.16.1.0", {"center": v(343.5, 20.67) * mm, "radius": 2.31 * mm});
            skCircle(sketch, "E51.16.2.0", {"center": v(343.5, 7.97) * mm, "radius": 2.31 * mm});
            skCircle(sketch, "E51.16.3.0", {"center": v(343.5, -4.73) * mm, "radius": 2.31 * mm});
            skCircle(sketch, "E51.16.4.0", {"center": v(343.5, -17.43) * mm, "radius": 2.31 * mm});
            skCircle(sketch, "E51.16.5.0", {"center": v(343.5, -30.13) * mm, "radius": 2.31 * mm});
            skCircle(sketch, "E51.16.6.0", {"center": v(343.5, -42.83) * mm, "radius": 2.31 * mm});
            skCircle(sketch, "E51.16.7.0", {"center": v(343.5, -55.53) * mm, "radius": 2.31 * mm});
            skCircle(sketch, "E51.16.8.0", {"center": v(343.5, -68.23) * mm, "radius": 2.31 * mm});
            skCircle(sketch, "E51.16.9.0", {"center": v(343.5, -80.93) * mm, "radius": 2.31 * mm});
            skCircle(sketch, "E51.16.10.0", {"center": v(343.5, -93.63) * mm, "radius": 2.31 * mm});
            skCircle(sketch, "E51.16.11.0", {"center": v(343.5, -106.33) * mm, "radius": 2.31 * mm});
            skCircle(sketch, "E51.16.12.0", {"center": v(343.5, -119.03) * mm, "radius": 2.31 * mm});
            skCircle(sketch, "E51.17.0.0", {"center": v(356.2, 33.37) * mm, "radius": 2.31 * mm});
            skCircle(sketch, "E51.17.1.0", {"center": v(356.2, 20.67) * mm, "radius": 2.31 * mm});
            skCircle(sketch, "E51.17.2.0", {"center": v(356.2, 7.97) * mm, "radius": 2.31 * mm});
            skCircle(sketch, "E51.17.3.0", {"center": v(356.2, -4.73) * mm, "radius": 2.31 * mm});
            skCircle(sketch, "E51.17.4.0", {"center": v(356.2, -17.43) * mm, "radius": 2.31 * mm});
            skCircle(sketch, "E51.17.5.0", {"center": v(356.2, -30.13) * mm, "radius": 2.31 * mm});
            skCircle(sketch, "E51.17.6.0", {"center": v(356.2, -42.83) * mm, "radius": 2.31 * mm});
            skCircle(sketch, "E51.17.7.0", {"center": v(356.2, -55.53) * mm, "radius": 2.31 * mm});
            skCircle(sketch, "E51.17.8.0", {"center": v(356.2, -68.23) * mm, "radius": 2.31 * mm});
            skCircle(sketch, "E51.17.9.0", {"center": v(356.2, -80.93) * mm, "radius": 2.31 * mm});
            skCircle(sketch, "E51.17.10.0", {"center": v(356.2, -93.63) * mm, "radius": 2.31 * mm});
            skCircle(sketch, "E51.17.11.0", {"center": v(356.2, -106.33) * mm, "radius": 2.31 * mm});
            skCircle(sketch, "E51.17.12.0", {"center": v(356.2, -119.03) * mm, "radius": 2.31 * mm});
            skCircle(sketch, "E51.18.0.0", {"center": v(368.9, 33.37) * mm, "radius": 2.31 * mm});
            skCircle(sketch, "E51.18.1.0", {"center": v(368.9, 20.67) * mm, "radius": 2.31 * mm});
            skCircle(sketch, "E51.18.2.0", {"center": v(368.9, 7.97) * mm, "radius": 2.31 * mm});
            skCircle(sketch, "E51.18.3.0", {"center": v(368.9, -4.73) * mm, "radius": 2.31 * mm});
            skCircle(sketch, "E51.18.4.0", {"center": v(368.9, -17.43) * mm, "radius": 2.31 * mm});
            skCircle(sketch, "E51.18.5.0", {"center": v(368.9, -30.13) * mm, "radius": 2.31 * mm});
            skCircle(sketch, "E51.18.6.0", {"center": v(368.9, -42.83) * mm, "radius": 2.31 * mm});
            skCircle(sketch, "E51.18.7.0", {"center": v(368.9, -55.53) * mm, "radius": 2.31 * mm});
            skCircle(sketch, "E51.18.8.0", {"center": v(368.9, -68.23) * mm, "radius": 2.31 * mm});
            skCircle(sketch, "E51.18.9.0", {"center": v(368.9, -80.93) * mm, "radius": 2.31 * mm});
            skCircle(sketch, "E51.18.10.0", {"center": v(368.9, -93.63) * mm, "radius": 2.31 * mm});
            skCircle(sketch, "E51.18.11.0", {"center": v(368.9, -106.33) * mm, "radius": 2.31 * mm});
            skCircle(sketch, "E51.18.12.0", {"center": v(368.9, -119.03) * mm, "radius": 2.31 * mm});
            skLineSegment(sketch, "E51.direction1", {"start": v(140.3, 33.37) * mm, "end": v(153, 33.37) * mm, "construction": true});
            skLineSegment(sketch, "E51.direction2", {"start": v(140.3, 33.37) * mm, "end": v(140.3, 20.67) * mm, "construction": true});
            const initialGuessF4  = {"E44": [0.205, -0.03926, 1, 0, 0.01179]};
            skSetInitialGuess(sketch, initialGuessF4);
            skSolve(sketch);
        }
        {
            var Q0;
            Q0 = qSketchRegion(id + "F4", true);
            extrude(context, id + "F5", {"entities" : qUnion([Q0]), "depth" : 3 * mm});
        }
    });
